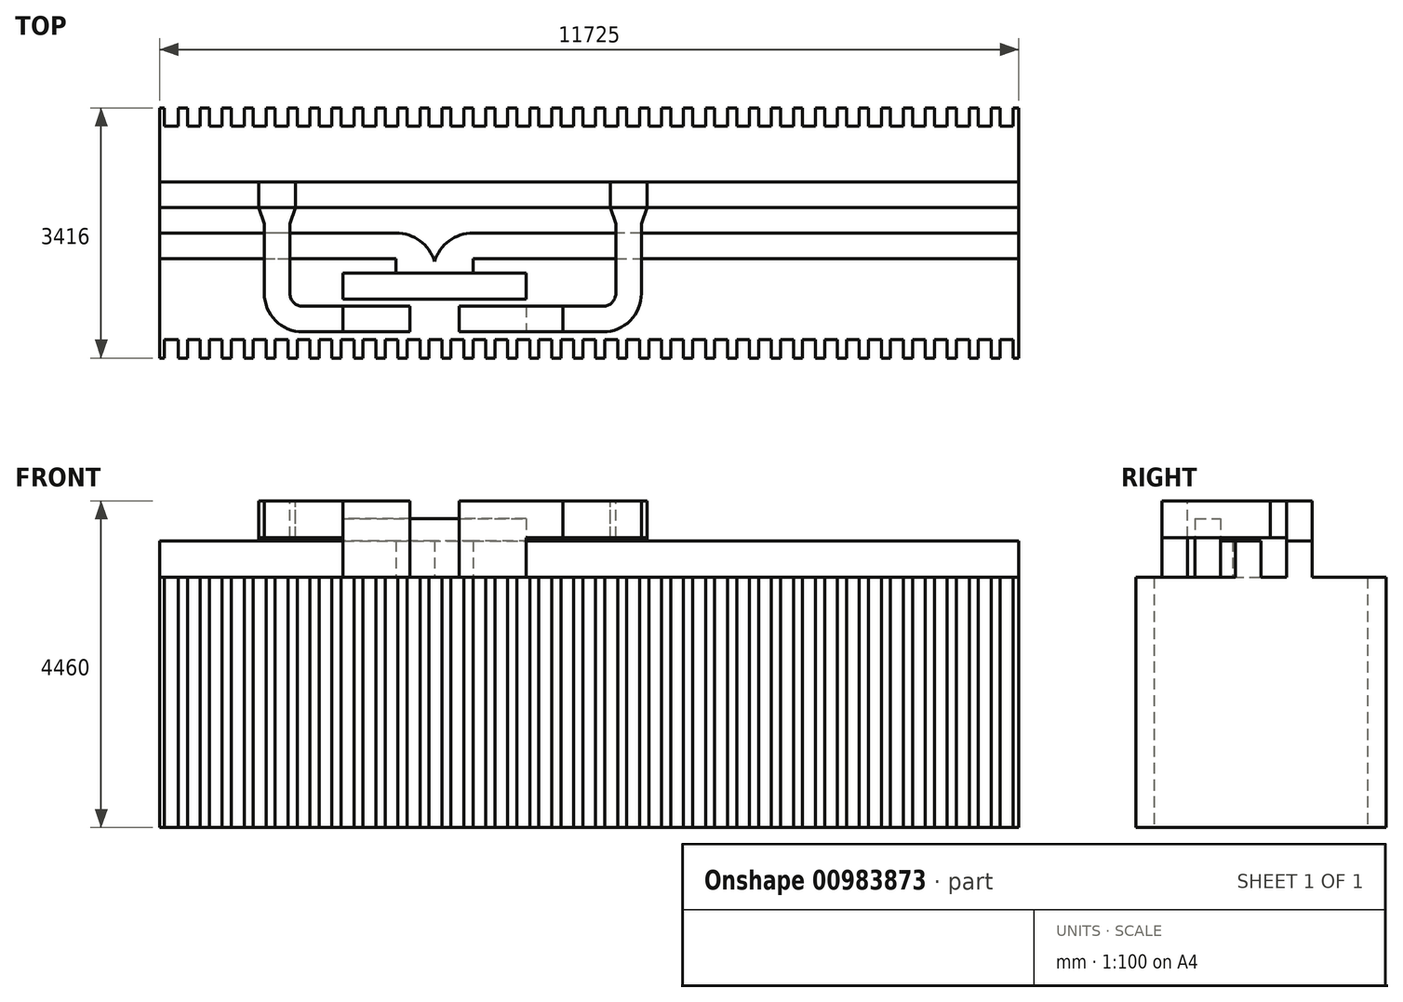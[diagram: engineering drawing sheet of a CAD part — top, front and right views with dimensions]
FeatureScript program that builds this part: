
annotation { "Feature Type Name" : "Feature", "Feature Type Description" : "" }
export const myFeature = defineFeature(function(context is Context, id is Id, definition is map)
    precondition{}
    {
        {
            var Q0;
            Q0=qCreatedBy(makeId("Top.planeOp"),FACE);
            var sketch = newSketch(context, id + "F0", { "sketchPlane" : qUnion([Q0])});
            skLineSegment(sketch, "E0.bottom", {"start": v(-25000, 7300) * mm, "end": v(25000, 7300) * mm});
            skLineSegment(sketch, "E0.top", {"start": v(-25000, -7300) * mm, "end": v(25000, -7300) * mm});
            skLineSegment(sketch, "E0.left", {"start": v(-25000, 7300) * mm, "end": v(-25000, -7300) * mm});
            skLineSegment(sketch, "E0.right", {"start": v(25000, 7300) * mm, "end": v(25000, -7300) * mm});
            skPoint(sketch, "E0.middle", {"position": v(0, 0) * mm});
            skSolve(sketch);
        }
        {
            var Q0;
            Q0=makeQuery(id+"F0.imprint","IMPRINT",FACE,{"disambiguationData":[TD([[makeQuery(id+"F0.imprint","IMPRINT",EDGE,{"derivedFrom":sQuery(id+"F0.wireOp",EDGE,"E0.bottom")}),-1.0]])]});
            var sketch = newSketch(context, id + "F1", { "sketchPlane" : qUnion([Q0])});
            skLineSegment(sketch, "E1", {"start": v(-20201.46, 5909) * mm, "end": v(-20138.96, 5909) * mm});
            skLineSegment(sketch, "E2", {"start": v(-20201.46, 5909) * mm, "end": v(-20201.46, 2493) * mm});
            skLineSegment(sketch, "E3", {"start": v(-20201.46, 2493) * mm, "end": v(-20138.96, 2493) * mm});
            skLineSegment(sketch, "E4", {"start": v(-8476.46, 2493) * mm, "end": v(-8476.46, 5909) * mm});
            skLineSegment(sketch, "E5.0", {"start": v(-20138.96, 5909) * mm, "end": v(-20138.96, 2493) * mm});
            skLineSegment(sketch, "E6.0", {"start": v(-19951.46, 5909) * mm, "end": v(-19951.46, 2493) * mm});
            skLineSegment(sketch, "E7.0", {"start": v(-19651.46, 5909) * mm, "end": v(-19651.46, 2493) * mm});
            skLineSegment(sketch, "E8.0", {"start": v(-19351.46, 5909) * mm, "end": v(-19351.46, 2493) * mm});
            skLineSegment(sketch, "E9.0", {"start": v(-19051.46, 5909) * mm, "end": v(-19051.46, 2493) * mm});
            skLineSegment(sketch, "E10.0", {"start": v(-18751.46, 5909) * mm, "end": v(-18751.46, 2493) * mm});
            skLineSegment(sketch, "E11.0", {"start": v(-18451.46, 5909) * mm, "end": v(-18451.46, 2493) * mm});
            skLineSegment(sketch, "E12.0", {"start": v(-18151.46, 5909) * mm, "end": v(-18151.46, 2493) * mm});
            skLineSegment(sketch, "E13.0", {"start": v(-17851.46, 5909) * mm, "end": v(-17851.46, 2493) * mm});
            skLineSegment(sketch, "E14.0", {"start": v(-17551.46, 5909) * mm, "end": v(-17551.46, 2493) * mm});
            skLineSegment(sketch, "E15.0", {"start": v(-17251.46, 5909) * mm, "end": v(-17251.46, 2493) * mm});
            skLineSegment(sketch, "E16.0", {"start": v(-16951.46, 5909) * mm, "end": v(-16951.46, 2493) * mm});
            skLineSegment(sketch, "E17.0", {"start": v(-16651.46, 5909) * mm, "end": v(-16651.46, 2493) * mm});
            skLineSegment(sketch, "E18.0", {"start": v(-16351.46, 5909) * mm, "end": v(-16351.46, 2493) * mm});
            skLineSegment(sketch, "E19.0", {"start": v(-16051.46, 5909) * mm, "end": v(-16051.46, 2493) * mm});
            skLineSegment(sketch, "E20.0", {"start": v(-15751.46, 5909) * mm, "end": v(-15751.46, 2493) * mm});
            skLineSegment(sketch, "E21.0", {"start": v(-25005, 7305) * mm, "end": v(-25005, -7305) * mm});
            skLineSegment(sketch, "E21.1", {"start": v(25005, 7305) * mm, "end": v(-25005, 7305) * mm});
            skLineSegment(sketch, "E21.2", {"start": v(25005, -7305) * mm, "end": v(25005, 7305) * mm});
            skLineSegment(sketch, "E21.3", {"start": v(-25005, -7305) * mm, "end": v(25005, -7305) * mm});
            skLineSegment(sketch, "E22.0", {"start": v(-15451.46, 5909) * mm, "end": v(-15451.46, 2493) * mm});
            skLineSegment(sketch, "E23.0", {"start": v(-15151.46, 5909) * mm, "end": v(-15151.46, 2493) * mm});
            skLineSegment(sketch, "E24.0", {"start": v(-14851.46, 5909) * mm, "end": v(-14851.46, 2493) * mm});
            skLineSegment(sketch, "E25.0", {"start": v(-14551.46, 5909) * mm, "end": v(-14551.46, 2493) * mm});
            skLineSegment(sketch, "E26.0", {"start": v(-14251.46, 5909) * mm, "end": v(-14251.46, 2493) * mm});
            skLineSegment(sketch, "E27.0", {"start": v(-13951.46, 5909) * mm, "end": v(-13951.46, 2493) * mm});
            skLineSegment(sketch, "E28.0", {"start": v(-13651.46, 5909) * mm, "end": v(-13651.46, 2493) * mm});
            skLineSegment(sketch, "E29.0", {"start": v(-13351.46, 5909) * mm, "end": v(-13351.46, 2493) * mm});
            skLineSegment(sketch, "E30.0", {"start": v(-13051.46, 5909) * mm, "end": v(-13051.46, 2493) * mm});
            skLineSegment(sketch, "E31.0", {"start": v(-12751.46, 5909) * mm, "end": v(-12751.46, 2493) * mm});
            skLineSegment(sketch, "E32.0", {"start": v(-12451.46, 5909) * mm, "end": v(-12451.46, 2493) * mm});
            skLineSegment(sketch, "E33.0", {"start": v(-12151.46, 5909) * mm, "end": v(-12151.46, 2493) * mm});
            skLineSegment(sketch, "E34.0", {"start": v(-11851.46, 5909) * mm, "end": v(-11851.46, 2493) * mm});
            skLineSegment(sketch, "E35.0", {"start": v(-11551.46, 5909) * mm, "end": v(-11551.46, 2493) * mm});
            skLineSegment(sketch, "E36.0", {"start": v(-11251.46, 5909) * mm, "end": v(-11251.46, 2493) * mm});
            skLineSegment(sketch, "E37.0", {"start": v(-10951.46, 5909) * mm, "end": v(-10951.46, 2493) * mm});
            skLineSegment(sketch, "E38.0", {"start": v(-10651.46, 5909) * mm, "end": v(-10651.46, 2493) * mm});
            skLineSegment(sketch, "E39.0", {"start": v(-10351.46, 5909) * mm, "end": v(-10351.46, 2493) * mm});
            skLineSegment(sketch, "E40.0", {"start": v(-10051.46, 5909) * mm, "end": v(-10051.46, 2493) * mm});
            skLineSegment(sketch, "E41.0", {"start": v(-9751.46, 5909) * mm, "end": v(-9751.46, 2493) * mm});
            skLineSegment(sketch, "E42.0", {"start": v(-9451.46, 5909) * mm, "end": v(-9451.46, 2493) * mm});
            skLineSegment(sketch, "E43.0", {"start": v(-9151.46, 5909) * mm, "end": v(-9151.46, 2493) * mm});
            skLineSegment(sketch, "E44.0", {"start": v(-8851.46, 5909) * mm, "end": v(-8851.46, 2493) * mm});
            skLineSegment(sketch, "E45.0", {"start": v(-8551.46, 5909) * mm, "end": v(-8551.46, 2493) * mm});
            skLineSegment(sketch, "E46.0", {"start": v(-19826.46, 5909) * mm, "end": v(-19826.46, 2493) * mm});
            skLineSegment(sketch, "E47.0", {"start": v(-19526.46, 5909) * mm, "end": v(-19526.46, 2493) * mm});
            skLineSegment(sketch, "E48.0", {"start": v(-19226.46, 5909) * mm, "end": v(-19226.46, 2493) * mm});
            skLineSegment(sketch, "E49.0", {"start": v(-18926.46, 5909) * mm, "end": v(-18926.46, 2493) * mm});
            skLineSegment(sketch, "E50.0", {"start": v(-18626.46, 5909) * mm, "end": v(-18626.46, 2493) * mm});
            skLineSegment(sketch, "E51.0", {"start": v(-18326.46, 5909) * mm, "end": v(-18326.46, 2493) * mm});
            skLineSegment(sketch, "E52.0", {"start": v(-18026.46, 5909) * mm, "end": v(-18026.46, 2493) * mm});
            skLineSegment(sketch, "E53.0", {"start": v(-17726.46, 5909) * mm, "end": v(-17726.46, 2493) * mm});
            skLineSegment(sketch, "E54.0", {"start": v(-17426.46, 5909) * mm, "end": v(-17426.46, 2493) * mm});
            skLineSegment(sketch, "E55.0", {"start": v(-17126.46, 5909) * mm, "end": v(-17126.46, 2493) * mm});
            skLineSegment(sketch, "E56.0", {"start": v(-16826.46, 5909) * mm, "end": v(-16826.46, 2493) * mm});
            skLineSegment(sketch, "E57.0", {"start": v(-16526.46, 5909) * mm, "end": v(-16526.46, 2493) * mm});
            skLineSegment(sketch, "E58.0", {"start": v(-16226.46, 5909) * mm, "end": v(-16226.46, 2493) * mm});
            skLineSegment(sketch, "E59.0", {"start": v(-15926.46, 5909) * mm, "end": v(-15926.46, 2493) * mm});
            skLineSegment(sketch, "E60.0", {"start": v(-15626.46, 5909) * mm, "end": v(-15626.46, 2493) * mm});
            skLineSegment(sketch, "E61.0", {"start": v(-15326.46, 5909) * mm, "end": v(-15326.46, 2493) * mm});
            skLineSegment(sketch, "E62.0", {"start": v(-15026.46, 5909) * mm, "end": v(-15026.46, 2493) * mm});
            skLineSegment(sketch, "E63.0", {"start": v(-14726.46, 5909) * mm, "end": v(-14726.46, 2493) * mm});
            skLineSegment(sketch, "E64.0", {"start": v(-14426.46, 5909) * mm, "end": v(-14426.46, 2493) * mm});
            skLineSegment(sketch, "E65.0", {"start": v(-14126.46, 5909) * mm, "end": v(-14126.46, 2493) * mm});
            skLineSegment(sketch, "E66.0", {"start": v(-13826.46, 5909) * mm, "end": v(-13826.46, 2493) * mm});
            skLineSegment(sketch, "E67.0", {"start": v(-13526.46, 5909) * mm, "end": v(-13526.46, 2493) * mm});
            skLineSegment(sketch, "E68.0", {"start": v(-13226.46, 5909) * mm, "end": v(-13226.46, 2493) * mm});
            skLineSegment(sketch, "E69.0", {"start": v(-12926.46, 5909) * mm, "end": v(-12926.46, 2493) * mm});
            skLineSegment(sketch, "E70.0", {"start": v(-12626.46, 5909) * mm, "end": v(-12626.46, 2493) * mm});
            skLineSegment(sketch, "E71.0", {"start": v(-12326.46, 5909) * mm, "end": v(-12326.46, 2493) * mm});
            skLineSegment(sketch, "E72.0", {"start": v(-12026.46, 5909) * mm, "end": v(-12026.46, 2493) * mm});
            skLineSegment(sketch, "E73.0", {"start": v(-11726.46, 5909) * mm, "end": v(-11726.46, 2493) * mm});
            skLineSegment(sketch, "E74.0", {"start": v(-11426.46, 5909) * mm, "end": v(-11426.46, 2493) * mm});
            skLineSegment(sketch, "E75.0", {"start": v(-11126.46, 5909) * mm, "end": v(-11126.46, 2493) * mm});
            skLineSegment(sketch, "E76.0", {"start": v(-10826.46, 5909) * mm, "end": v(-10826.46, 2493) * mm});
            skLineSegment(sketch, "E77.0", {"start": v(-10526.46, 5909) * mm, "end": v(-10526.46, 2493) * mm});
            skLineSegment(sketch, "E78.0", {"start": v(-10226.46, 5909) * mm, "end": v(-10226.46, 2493) * mm});
            skLineSegment(sketch, "E79.0", {"start": v(-9926.46, 5909) * mm, "end": v(-9926.46, 2493) * mm});
            skLineSegment(sketch, "E80.0", {"start": v(-9626.46, 5909) * mm, "end": v(-9626.46, 2493) * mm});
            skLineSegment(sketch, "E81.0", {"start": v(-9326.46, 5909) * mm, "end": v(-9326.46, 2493) * mm});
            skLineSegment(sketch, "E82.0", {"start": v(-9026.46, 5909) * mm, "end": v(-9026.46, 2493) * mm});
            skLineSegment(sketch, "E83.0", {"start": v(-8726.46, 5909) * mm, "end": v(-8726.46, 2493) * mm});
            skLineSegment(sketch, "E84", {"start": v(-20201.46, 5659) * mm, "end": v(-8476.46, 5659) * mm});
            skLineSegment(sketch, "E85", {"start": v(-20201.46, 2743) * mm, "end": v(-8476.46, 2743) * mm});
            skLineSegment(sketch, "E86.trimOffspring", {"start": v(-8551.46, 5909) * mm, "end": v(-8476.46, 5909) * mm});
            skLineSegment(sketch, "E87.trimOffspring", {"start": v(-8851.46, 5909) * mm, "end": v(-8726.46, 5909) * mm});
            skLineSegment(sketch, "E88.trimOffspring", {"start": v(-9151.46, 5909) * mm, "end": v(-9026.46, 5909) * mm});
            skLineSegment(sketch, "E89.trimOffspring", {"start": v(-9451.46, 5909) * mm, "end": v(-9326.46, 5909) * mm});
            skLineSegment(sketch, "E90.trimOffspring", {"start": v(-9751.46, 5909) * mm, "end": v(-9626.46, 5909) * mm});
            skLineSegment(sketch, "E91.trimOffspring", {"start": v(-10051.46, 5909) * mm, "end": v(-9926.46, 5909) * mm});
            skLineSegment(sketch, "E92.trimOffspring", {"start": v(-10351.46, 5909) * mm, "end": v(-10226.46, 5909) * mm});
            skLineSegment(sketch, "E93.trimOffspring", {"start": v(-10651.46, 5909) * mm, "end": v(-10526.46, 5909) * mm});
            skLineSegment(sketch, "E94.trimOffspring", {"start": v(-10951.46, 5909) * mm, "end": v(-10826.46, 5909) * mm});
            skLineSegment(sketch, "E95.trimOffspring", {"start": v(-11251.46, 5909) * mm, "end": v(-11126.46, 5909) * mm});
            skLineSegment(sketch, "E96.trimOffspring", {"start": v(-11551.46, 5909) * mm, "end": v(-11426.46, 5909) * mm});
            skLineSegment(sketch, "E97.trimOffspring", {"start": v(-11851.46, 5909) * mm, "end": v(-11726.46, 5909) * mm});
            skLineSegment(sketch, "E98.trimOffspring", {"start": v(-12151.46, 5909) * mm, "end": v(-12026.46, 5909) * mm});
            skLineSegment(sketch, "E99.trimOffspring", {"start": v(-12451.46, 5909) * mm, "end": v(-12326.46, 5909) * mm});
            skLineSegment(sketch, "E100.trimOffspring", {"start": v(-12751.46, 5909) * mm, "end": v(-12626.46, 5909) * mm});
            skLineSegment(sketch, "E101.trimOffspring", {"start": v(-13051.46, 5909) * mm, "end": v(-12926.46, 5909) * mm});
            skLineSegment(sketch, "E102.trimOffspring", {"start": v(-13351.46, 5909) * mm, "end": v(-13226.46, 5909) * mm});
            skLineSegment(sketch, "E103.trimOffspring", {"start": v(-13651.46, 5909) * mm, "end": v(-13526.46, 5909) * mm});
            skLineSegment(sketch, "E104.trimOffspring", {"start": v(-13951.46, 5909) * mm, "end": v(-13826.46, 5909) * mm});
            skLineSegment(sketch, "E105.trimOffspring", {"start": v(-14251.46, 5909) * mm, "end": v(-14126.46, 5909) * mm});
            skLineSegment(sketch, "E106.trimOffspring", {"start": v(-14551.46, 5909) * mm, "end": v(-14426.46, 5909) * mm});
            skLineSegment(sketch, "E107.trimOffspring", {"start": v(-14851.46, 5909) * mm, "end": v(-14726.46, 5909) * mm});
            skLineSegment(sketch, "E108.trimOffspring", {"start": v(-15151.46, 5909) * mm, "end": v(-15026.46, 5909) * mm});
            skLineSegment(sketch, "E109.trimOffspring", {"start": v(-15451.46, 5909) * mm, "end": v(-15326.46, 5909) * mm});
            skLineSegment(sketch, "E110.trimOffspring", {"start": v(-15751.46, 5909) * mm, "end": v(-15626.46, 5909) * mm});
            skLineSegment(sketch, "E111.trimOffspring", {"start": v(-16051.46, 5909) * mm, "end": v(-15926.46, 5909) * mm});
            skLineSegment(sketch, "E112.trimOffspring", {"start": v(-16351.46, 5909) * mm, "end": v(-16226.46, 5909) * mm});
            skLineSegment(sketch, "E113.trimOffspring", {"start": v(-16651.46, 5909) * mm, "end": v(-16526.46, 5909) * mm});
            skLineSegment(sketch, "E114.trimOffspring", {"start": v(-16951.46, 5909) * mm, "end": v(-16826.46, 5909) * mm});
            skLineSegment(sketch, "E115.trimOffspring", {"start": v(-17251.46, 5909) * mm, "end": v(-17126.46, 5909) * mm});
            skLineSegment(sketch, "E116.trimOffspring", {"start": v(-17551.46, 5909) * mm, "end": v(-17426.46, 5909) * mm});
            skLineSegment(sketch, "E117.trimOffspring", {"start": v(-17851.46, 5909) * mm, "end": v(-17726.46, 5909) * mm});
            skLineSegment(sketch, "E118.trimOffspring", {"start": v(-18151.46, 5909) * mm, "end": v(-18026.46, 5909) * mm});
            skLineSegment(sketch, "E119.trimOffspring", {"start": v(-18451.46, 5909) * mm, "end": v(-18326.46, 5909) * mm});
            skLineSegment(sketch, "E120.trimOffspring", {"start": v(-18751.46, 5909) * mm, "end": v(-18626.46, 5909) * mm});
            skLineSegment(sketch, "E121.trimOffspring", {"start": v(-19051.46, 5909) * mm, "end": v(-18926.46, 5909) * mm});
            skLineSegment(sketch, "E122.trimOffspring", {"start": v(-19351.46, 5909) * mm, "end": v(-19226.46, 5909) * mm});
            skLineSegment(sketch, "E123.trimOffspring", {"start": v(-19651.46, 5909) * mm, "end": v(-19526.46, 5909) * mm});
            skLineSegment(sketch, "E124.trimOffspring", {"start": v(-19951.46, 5909) * mm, "end": v(-19826.46, 5909) * mm});
            skLineSegment(sketch, "E125.trimOffspring", {"start": v(-19651.46, 2493) * mm, "end": v(-19526.46, 2493) * mm});
            skLineSegment(sketch, "E126.trimOffspring", {"start": v(-18751.46, 2493) * mm, "end": v(-18626.46, 2493) * mm});
            skLineSegment(sketch, "E127.trimOffspring", {"start": v(-17851.46, 2493) * mm, "end": v(-17726.46, 2493) * mm});
            skLineSegment(sketch, "E128.trimOffspring", {"start": v(-17251.46, 2493) * mm, "end": v(-17126.46, 2493) * mm});
            skLineSegment(sketch, "E129.trimOffspring", {"start": v(-16351.46, 2493) * mm, "end": v(-16226.46, 2493) * mm});
            skLineSegment(sketch, "E130.trimOffspring", {"start": v(-16951.46, 2493) * mm, "end": v(-16826.46, 2493) * mm});
            skLineSegment(sketch, "E131", {"start": v(-17551.46, 2493) * mm, "end": v(-17426.46, 2493) * mm});
            skLineSegment(sketch, "E132", {"start": v(-16651.46, 2493) * mm, "end": v(-16526.46, 2493) * mm});
            skLineSegment(sketch, "E133.trimOffspring", {"start": v(-15751.46, 2493) * mm, "end": v(-15626.46, 2493) * mm});
            skLineSegment(sketch, "E134.trimOffspring", {"start": v(-14551.46, 2493) * mm, "end": v(-14426.46, 2493) * mm});
            skLineSegment(sketch, "E135.trimOffspring", {"start": v(-15151.46, 2493) * mm, "end": v(-15026.46, 2493) * mm});
            skLineSegment(sketch, "E136.trimOffspring", {"start": v(-15451.46, 2493) * mm, "end": v(-15326.46, 2493) * mm});
            skLineSegment(sketch, "E137", {"start": v(-14851.46, 2493) * mm, "end": v(-14726.46, 2493) * mm});
            skLineSegment(sketch, "E138.trimOffspring", {"start": v(-13951.46, 2493) * mm, "end": v(-13826.46, 2493) * mm});
            skLineSegment(sketch, "E139.trimOffspring", {"start": v(-13351.46, 2493) * mm, "end": v(-13226.46, 2493) * mm});
            skLineSegment(sketch, "E140.trimOffspring", {"start": v(-13651.46, 2493) * mm, "end": v(-13526.46, 2493) * mm});
            skLineSegment(sketch, "E141", {"start": v(-14251.46, 2493) * mm, "end": v(-14126.46, 2493) * mm});
            skLineSegment(sketch, "E142.trimOffspring", {"start": v(-13051.46, 2493) * mm, "end": v(-12926.46, 2493) * mm});
            skLineSegment(sketch, "E143.trimOffspring", {"start": v(-12751.46, 2493) * mm, "end": v(-12626.46, 2493) * mm});
            skLineSegment(sketch, "E144.trimOffspring", {"start": v(-12151.46, 2493) * mm, "end": v(-12026.46, 2493) * mm});
            skLineSegment(sketch, "E145.trimOffspring", {"start": v(-11551.46, 2493) * mm, "end": v(-11426.46, 2493) * mm});
            skLineSegment(sketch, "E146.trimOffspring", {"start": v(-11851.46, 2493) * mm, "end": v(-11726.46, 2493) * mm});
            skLineSegment(sketch, "E147.trimOffspring", {"start": v(-11251.46, 2493) * mm, "end": v(-11126.46, 2493) * mm});
            skLineSegment(sketch, "E148.trimOffspring", {"start": v(-10951.46, 2493) * mm, "end": v(-10826.46, 2493) * mm});
            skLineSegment(sketch, "E149.trimOffspring", {"start": v(-10651.46, 2493) * mm, "end": v(-10526.46, 2493) * mm});
            skLineSegment(sketch, "E150.trimOffspring", {"start": v(-9751.46, 2493) * mm, "end": v(-9626.46, 2493) * mm});
            skLineSegment(sketch, "E151.trimOffspring", {"start": v(-8851.46, 2493) * mm, "end": v(-8726.46, 2493) * mm});
            skLineSegment(sketch, "E152", {"start": v(-10351.46, 2493) * mm, "end": v(-10226.46, 2493) * mm});
            skLineSegment(sketch, "E153", {"start": v(-10051.46, 2493) * mm, "end": v(-9926.46, 2493) * mm});
            skLineSegment(sketch, "E154", {"start": v(-9151.46, 2493) * mm, "end": v(-9026.46, 2493) * mm});
            skLineSegment(sketch, "E155.trimOffspring", {"start": v(-9451.46, 2493) * mm, "end": v(-9326.46, 2493) * mm});
            skLineSegment(sketch, "E156.trimOffspring", {"start": v(-8551.46, 2493) * mm, "end": v(-8476.46, 2493) * mm});
            skLineSegment(sketch, "E157.trimOffspring", {"start": v(-18451.46, 2493) * mm, "end": v(-18326.46, 2493) * mm});
            skLineSegment(sketch, "E158.trimOffspring", {"start": v(-19351.46, 2493) * mm, "end": v(-19226.46, 2493) * mm});
            skLineSegment(sketch, "E159", {"start": v(-19051.46, 2493) * mm, "end": v(-18926.46, 2493) * mm});
            skLineSegment(sketch, "E160", {"start": v(-18151.46, 2493) * mm, "end": v(-18026.46, 2493) * mm});
            skLineSegment(sketch, "E161", {"start": v(-16051.46, 2493) * mm, "end": v(-15926.46, 2493) * mm});
            skLineSegment(sketch, "E162", {"start": v(-19951.46, 2493) * mm, "end": v(-19826.46, 2493) * mm});
            skLineSegment(sketch, "E163", {"start": v(-12451.46, 2493) * mm, "end": v(-12326.46, 2493) * mm});
            skSolve(sketch);
        }
        {
            var Q0;
            {var subQ0=sQuery(id+"F1.wireOp",EDGE,"E88.trimOffspring");Q0=makeQuery(id+"F1.imprint","IMPRINT",FACE,{"disambiguationData":[TD([[makeQuery(id+"F1.imprint","IMPRINT",EDGE,{"derivedFrom":subQ0}),-1.0]])]});}
            var Q1;
            {var subQ0=sQuery(id+"F1.wireOp",EDGE,"E112.trimOffspring");Q1=makeQuery(id+"F1.imprint","IMPRINT",FACE,{"disambiguationData":[TD([[makeQuery(id+"F1.imprint","IMPRINT",EDGE,{"derivedFrom":subQ0}),-1.0]])]});}
            var Q2;
            {var subQ0=sQuery(id+"F1.wireOp",EDGE,"E84");var subQ1=sQuery(id+"F1.wireOp",EDGE,"E38.0");var subQ2=makeQuery(id+"F1.imprint","INTERSECT",VERTEX,{"derivedFrom":[subQ1,subQ0]});Q2=makeQuery(id+"F1.imprint","IMPRINT",FACE,{"disambiguationData":[TD([[makeQuery(id+"F1.imprint","IMPRINT",EDGE,{"disambiguationData":[TD([[subQ2,-1.0]])],"derivedFrom":subQ1}),1.0]])]});}
            var Q3;
            {var subQ0=sQuery(id+"F1.wireOp",EDGE,"E158.trimOffspring");Q3=makeQuery(id+"F1.imprint","IMPRINT",FACE,{"disambiguationData":[TD([[makeQuery(id+"F1.imprint","IMPRINT",EDGE,{"derivedFrom":subQ0}),1.0]])]});}
            var Q4;
            {var subQ0=sQuery(id+"F1.wireOp",EDGE,"E84");var subQ1=sQuery(id+"F1.wireOp",EDGE,"E18.0");var subQ2=makeQuery(id+"F1.imprint","INTERSECT",VERTEX,{"derivedFrom":[subQ1,subQ0]});Q4=makeQuery(id+"F1.imprint","IMPRINT",FACE,{"disambiguationData":[TD([[makeQuery(id+"F1.imprint","IMPRINT",EDGE,{"disambiguationData":[TD([[subQ2,-1.0]])],"derivedFrom":subQ1}),-1.0]])]});}
            var Q5;
            {var subQ0=sQuery(id+"F1.wireOp",EDGE,"E140.trimOffspring");Q5=makeQuery(id+"F1.imprint","IMPRINT",FACE,{"disambiguationData":[TD([[makeQuery(id+"F1.imprint","IMPRINT",EDGE,{"derivedFrom":subQ0}),1.0]])]});}
            var Q6;
            {var subQ0=sQuery(id+"F1.wireOp",EDGE,"E84");var subQ1=sQuery(id+"F1.wireOp",EDGE,"E35.0");var subQ2=makeQuery(id+"F1.imprint","INTERSECT",VERTEX,{"derivedFrom":[subQ1,subQ0]});Q6=makeQuery(id+"F1.imprint","IMPRINT",FACE,{"disambiguationData":[TD([[makeQuery(id+"F1.imprint","IMPRINT",EDGE,{"disambiguationData":[TD([[subQ2,-1.0]])],"derivedFrom":subQ1}),-1.0]])]});}
            var Q7;
            {var subQ0=sQuery(id+"F1.wireOp",EDGE,"E107.trimOffspring");Q7=makeQuery(id+"F1.imprint","IMPRINT",FACE,{"disambiguationData":[TD([[makeQuery(id+"F1.imprint","IMPRINT",EDGE,{"derivedFrom":subQ0}),-1.0]])]});}
            var Q8;
            {var subQ0=sQuery(id+"F1.wireOp",EDGE,"E129.trimOffspring");Q8=makeQuery(id+"F1.imprint","IMPRINT",FACE,{"disambiguationData":[TD([[makeQuery(id+"F1.imprint","IMPRINT",EDGE,{"derivedFrom":subQ0}),1.0]])]});}
            var Q9;
            {var subQ0=sQuery(id+"F1.wireOp",EDGE,"E120.trimOffspring");Q9=makeQuery(id+"F1.imprint","IMPRINT",FACE,{"disambiguationData":[TD([[makeQuery(id+"F1.imprint","IMPRINT",EDGE,{"derivedFrom":subQ0}),-1.0]])]});}
            var Q10;
            {var subQ0=sQuery(id+"F1.wireOp",EDGE,"E115.trimOffspring");Q10=makeQuery(id+"F1.imprint","IMPRINT",FACE,{"disambiguationData":[TD([[makeQuery(id+"F1.imprint","IMPRINT",EDGE,{"derivedFrom":subQ0}),-1.0]])]});}
            var Q11;
            {var subQ0=sQuery(id+"F1.wireOp",EDGE,"E138.trimOffspring");Q11=makeQuery(id+"F1.imprint","IMPRINT",FACE,{"disambiguationData":[TD([[makeQuery(id+"F1.imprint","IMPRINT",EDGE,{"derivedFrom":subQ0}),1.0]])]});}
            var Q12;
            {var subQ0=sQuery(id+"F1.wireOp",EDGE,"E84");var subQ1=sQuery(id+"F1.wireOp",EDGE,"E11.0");var subQ2=makeQuery(id+"F1.imprint","INTERSECT",VERTEX,{"derivedFrom":[subQ1,subQ0]});Q12=makeQuery(id+"F1.imprint","IMPRINT",FACE,{"disambiguationData":[TD([[makeQuery(id+"F1.imprint","IMPRINT",EDGE,{"disambiguationData":[TD([[subQ2,-1.0]])],"derivedFrom":subQ1}),1.0]])]});}
            var Q13;
            {var subQ0=sQuery(id+"F1.wireOp",EDGE,"E91.trimOffspring");Q13=makeQuery(id+"F1.imprint","IMPRINT",FACE,{"disambiguationData":[TD([[makeQuery(id+"F1.imprint","IMPRINT",EDGE,{"derivedFrom":subQ0}),-1.0]])]});}
            var Q14;
            {var subQ0=sQuery(id+"F1.wireOp",EDGE,"E84");var subQ1=sQuery(id+"F1.wireOp",EDGE,"E13.0");var subQ2=makeQuery(id+"F1.imprint","INTERSECT",VERTEX,{"derivedFrom":[subQ1,subQ0]});Q14=makeQuery(id+"F1.imprint","IMPRINT",FACE,{"disambiguationData":[TD([[makeQuery(id+"F1.imprint","IMPRINT",EDGE,{"disambiguationData":[TD([[subQ2,-1.0]])],"derivedFrom":subQ1}),-1.0]])]});}
            var Q15;
            {var subQ0=sQuery(id+"F1.wireOp",EDGE,"E84");var subQ1=sQuery(id+"F1.wireOp",EDGE,"E26.0");var subQ2=makeQuery(id+"F1.imprint","INTERSECT",VERTEX,{"derivedFrom":[subQ1,subQ0]});Q15=makeQuery(id+"F1.imprint","IMPRINT",FACE,{"disambiguationData":[TD([[makeQuery(id+"F1.imprint","IMPRINT",EDGE,{"disambiguationData":[TD([[subQ2,-1.0]])],"derivedFrom":subQ1}),-1.0]])]});}
            var Q16;
            {var subQ0=sQuery(id+"F1.wireOp",EDGE,"E121.trimOffspring");Q16=makeQuery(id+"F1.imprint","IMPRINT",FACE,{"disambiguationData":[TD([[makeQuery(id+"F1.imprint","IMPRINT",EDGE,{"derivedFrom":subQ0}),-1.0]])]});}
            var Q17;
            {var subQ0=sQuery(id+"F1.wireOp",EDGE,"E130.trimOffspring");Q17=makeQuery(id+"F1.imprint","IMPRINT",FACE,{"disambiguationData":[TD([[makeQuery(id+"F1.imprint","IMPRINT",EDGE,{"derivedFrom":subQ0}),1.0]])]});}
            var Q18;
            {var subQ0=sQuery(id+"F1.wireOp",EDGE,"E154");Q18=makeQuery(id+"F1.imprint","IMPRINT",FACE,{"disambiguationData":[TD([[makeQuery(id+"F1.imprint","IMPRINT",EDGE,{"derivedFrom":subQ0}),1.0]])]});}
            var Q19;
            {var subQ0=sQuery(id+"F1.wireOp",EDGE,"E151.trimOffspring");Q19=makeQuery(id+"F1.imprint","IMPRINT",FACE,{"disambiguationData":[TD([[makeQuery(id+"F1.imprint","IMPRINT",EDGE,{"derivedFrom":subQ0}),1.0]])]});}
            var Q20;
            {var subQ0=sQuery(id+"F1.wireOp",EDGE,"E84");var subQ1=sQuery(id+"F1.wireOp",EDGE,"E30.0");var subQ2=makeQuery(id+"F1.imprint","INTERSECT",VERTEX,{"derivedFrom":[subQ1,subQ0]});Q20=makeQuery(id+"F1.imprint","IMPRINT",FACE,{"disambiguationData":[TD([[makeQuery(id+"F1.imprint","IMPRINT",EDGE,{"disambiguationData":[TD([[subQ2,-1.0]])],"derivedFrom":subQ1}),-1.0]])]});}
            var Q21;
            {var subQ0=sQuery(id+"F1.wireOp",EDGE,"E84");var subQ1=sQuery(id+"F1.wireOp",EDGE,"E19.0");var subQ2=makeQuery(id+"F1.imprint","INTERSECT",VERTEX,{"derivedFrom":[subQ1,subQ0]});Q21=makeQuery(id+"F1.imprint","IMPRINT",FACE,{"disambiguationData":[TD([[makeQuery(id+"F1.imprint","IMPRINT",EDGE,{"disambiguationData":[TD([[subQ2,-1.0]])],"derivedFrom":subQ1}),1.0]])]});}
            var Q22;
            {var subQ0=sQuery(id+"F1.wireOp",EDGE,"E84");var subQ1=sQuery(id+"F1.wireOp",EDGE,"E14.0");var subQ2=makeQuery(id+"F1.imprint","INTERSECT",VERTEX,{"derivedFrom":[subQ1,subQ0]});Q22=makeQuery(id+"F1.imprint","IMPRINT",FACE,{"disambiguationData":[TD([[makeQuery(id+"F1.imprint","IMPRINT",EDGE,{"disambiguationData":[TD([[subQ2,-1.0]])],"derivedFrom":subQ1}),-1.0]])]});}
            var Q23;
            {var subQ0=sQuery(id+"F1.wireOp",EDGE,"E84");var subQ1=sQuery(id+"F1.wireOp",EDGE,"E12.0");var subQ2=makeQuery(id+"F1.imprint","INTERSECT",VERTEX,{"derivedFrom":[subQ1,subQ0]});Q23=makeQuery(id+"F1.imprint","IMPRINT",FACE,{"disambiguationData":[TD([[makeQuery(id+"F1.imprint","IMPRINT",EDGE,{"disambiguationData":[TD([[subQ2,-1.0]])],"derivedFrom":subQ1}),1.0]])]});}
            var Q24;
            {var subQ0=sQuery(id+"F1.wireOp",EDGE,"E143.trimOffspring");Q24=makeQuery(id+"F1.imprint","IMPRINT",FACE,{"disambiguationData":[TD([[makeQuery(id+"F1.imprint","IMPRINT",EDGE,{"derivedFrom":subQ0}),1.0]])]});}
            var Q25;
            {var subQ0=sQuery(id+"F1.wireOp",EDGE,"E161");Q25=makeQuery(id+"F1.imprint","IMPRINT",FACE,{"disambiguationData":[TD([[makeQuery(id+"F1.imprint","IMPRINT",EDGE,{"derivedFrom":subQ0}),1.0]])]});}
            var Q26;
            {var subQ0=sQuery(id+"F1.wireOp",EDGE,"E100.trimOffspring");Q26=makeQuery(id+"F1.imprint","IMPRINT",FACE,{"disambiguationData":[TD([[makeQuery(id+"F1.imprint","IMPRINT",EDGE,{"derivedFrom":subQ0}),-1.0]])]});}
            var Q27;
            {var subQ0=sQuery(id+"F1.wireOp",EDGE,"E84");var subQ1=sQuery(id+"F1.wireOp",EDGE,"E15.0");var subQ2=makeQuery(id+"F1.imprint","INTERSECT",VERTEX,{"derivedFrom":[subQ1,subQ0]});Q27=makeQuery(id+"F1.imprint","IMPRINT",FACE,{"disambiguationData":[TD([[makeQuery(id+"F1.imprint","IMPRINT",EDGE,{"disambiguationData":[TD([[subQ2,-1.0]])],"derivedFrom":subQ1}),-1.0]])]});}
            var Q28;
            {var subQ0=sQuery(id+"F1.wireOp",EDGE,"E84");var subQ1=sQuery(id+"F1.wireOp",EDGE,"E39.0");var subQ2=makeQuery(id+"F1.imprint","INTERSECT",VERTEX,{"derivedFrom":[subQ1,subQ0]});Q28=makeQuery(id+"F1.imprint","IMPRINT",FACE,{"disambiguationData":[TD([[makeQuery(id+"F1.imprint","IMPRINT",EDGE,{"disambiguationData":[TD([[subQ2,-1.0]])],"derivedFrom":subQ1}),1.0]])]});}
            var Q29;
            {var subQ0=sQuery(id+"F1.wireOp",EDGE,"E84");var subQ1=sQuery(id+"F1.wireOp",EDGE,"E36.0");var subQ2=makeQuery(id+"F1.imprint","INTERSECT",VERTEX,{"derivedFrom":[subQ1,subQ0]});Q29=makeQuery(id+"F1.imprint","IMPRINT",FACE,{"disambiguationData":[TD([[makeQuery(id+"F1.imprint","IMPRINT",EDGE,{"disambiguationData":[TD([[subQ2,-1.0]])],"derivedFrom":subQ1}),1.0]])]});}
            var Q30;
            {var subQ0=sQuery(id+"F1.wireOp",EDGE,"E84");var subQ1=sQuery(id+"F1.wireOp",EDGE,"E40.0");var subQ2=makeQuery(id+"F1.imprint","INTERSECT",VERTEX,{"derivedFrom":[subQ1,subQ0]});Q30=makeQuery(id+"F1.imprint","IMPRINT",FACE,{"disambiguationData":[TD([[makeQuery(id+"F1.imprint","IMPRINT",EDGE,{"disambiguationData":[TD([[subQ2,-1.0]])],"derivedFrom":subQ1}),1.0]])]});}
            var Q31;
            {var subQ0=sQuery(id+"F1.wireOp",EDGE,"E118.trimOffspring");Q31=makeQuery(id+"F1.imprint","IMPRINT",FACE,{"disambiguationData":[TD([[makeQuery(id+"F1.imprint","IMPRINT",EDGE,{"derivedFrom":subQ0}),-1.0]])]});}
            var Q32;
            {var subQ0=sQuery(id+"F1.wireOp",EDGE,"E84");var subQ1=sQuery(id+"F1.wireOp",EDGE,"E10.0");var subQ2=makeQuery(id+"F1.imprint","INTERSECT",VERTEX,{"derivedFrom":[subQ1,subQ0]});Q32=makeQuery(id+"F1.imprint","IMPRINT",FACE,{"disambiguationData":[TD([[makeQuery(id+"F1.imprint","IMPRINT",EDGE,{"disambiguationData":[TD([[subQ2,-1.0]])],"derivedFrom":subQ1}),-1.0]])]});}
            var Q33;
            {var subQ0=sQuery(id+"F1.wireOp",EDGE,"E84");var subQ1=sQuery(id+"F1.wireOp",EDGE,"E19.0");var subQ2=makeQuery(id+"F1.imprint","INTERSECT",VERTEX,{"derivedFrom":[subQ1,subQ0]});Q33=makeQuery(id+"F1.imprint","IMPRINT",FACE,{"disambiguationData":[TD([[makeQuery(id+"F1.imprint","IMPRINT",EDGE,{"disambiguationData":[TD([[subQ2,-1.0]])],"derivedFrom":subQ1}),-1.0]])]});}
            var Q34;
            {var subQ0=sQuery(id+"F1.wireOp",EDGE,"E84");var subQ1=sQuery(id+"F1.wireOp",EDGE,"E29.0");var subQ2=makeQuery(id+"F1.imprint","INTERSECT",VERTEX,{"derivedFrom":[subQ1,subQ0]});Q34=makeQuery(id+"F1.imprint","IMPRINT",FACE,{"disambiguationData":[TD([[makeQuery(id+"F1.imprint","IMPRINT",EDGE,{"disambiguationData":[TD([[subQ2,-1.0]])],"derivedFrom":subQ1}),-1.0]])]});}
            var Q35;
            {var subQ0=sQuery(id+"F1.wireOp",EDGE,"E84");var subQ1=sQuery(id+"F1.wireOp",EDGE,"E9.0");var subQ2=makeQuery(id+"F1.imprint","INTERSECT",VERTEX,{"derivedFrom":[subQ1,subQ0]});Q35=makeQuery(id+"F1.imprint","IMPRINT",FACE,{"disambiguationData":[TD([[makeQuery(id+"F1.imprint","IMPRINT",EDGE,{"disambiguationData":[TD([[subQ2,-1.0]])],"derivedFrom":subQ1}),-1.0]])]});}
            var Q36;
            {var subQ0=sQuery(id+"F1.wireOp",EDGE,"E102.trimOffspring");Q36=makeQuery(id+"F1.imprint","IMPRINT",FACE,{"disambiguationData":[TD([[makeQuery(id+"F1.imprint","IMPRINT",EDGE,{"derivedFrom":subQ0}),-1.0]])]});}
            var Q37;
            {var subQ0=sQuery(id+"F1.wireOp",EDGE,"E99.trimOffspring");Q37=makeQuery(id+"F1.imprint","IMPRINT",FACE,{"disambiguationData":[TD([[makeQuery(id+"F1.imprint","IMPRINT",EDGE,{"derivedFrom":subQ0}),-1.0]])]});}
            var Q38;
            {var subQ0=sQuery(id+"F1.wireOp",EDGE,"E117.trimOffspring");Q38=makeQuery(id+"F1.imprint","IMPRINT",FACE,{"disambiguationData":[TD([[makeQuery(id+"F1.imprint","IMPRINT",EDGE,{"derivedFrom":subQ0}),-1.0]])]});}
            var Q39;
            {var subQ0=sQuery(id+"F1.wireOp",EDGE,"E84");var subQ1=sQuery(id+"F1.wireOp",EDGE,"E17.0");var subQ2=makeQuery(id+"F1.imprint","INTERSECT",VERTEX,{"derivedFrom":[subQ1,subQ0]});Q39=makeQuery(id+"F1.imprint","IMPRINT",FACE,{"disambiguationData":[TD([[makeQuery(id+"F1.imprint","IMPRINT",EDGE,{"disambiguationData":[TD([[subQ2,-1.0]])],"derivedFrom":subQ1}),-1.0]])]});}
            var Q40;
            {var subQ0=sQuery(id+"F1.wireOp",EDGE,"E84");var subQ1=sQuery(id+"F1.wireOp",EDGE,"E33.0");var subQ2=makeQuery(id+"F1.imprint","INTERSECT",VERTEX,{"derivedFrom":[subQ1,subQ0]});Q40=makeQuery(id+"F1.imprint","IMPRINT",FACE,{"disambiguationData":[TD([[makeQuery(id+"F1.imprint","IMPRINT",EDGE,{"disambiguationData":[TD([[subQ2,-1.0]])],"derivedFrom":subQ1}),-1.0]])]});}
            var Q41;
            {var subQ0=sQuery(id+"F1.wireOp",EDGE,"E146.trimOffspring");Q41=makeQuery(id+"F1.imprint","IMPRINT",FACE,{"disambiguationData":[TD([[makeQuery(id+"F1.imprint","IMPRINT",EDGE,{"derivedFrom":subQ0}),1.0]])]});}
            var Q42;
            {var subQ0=sQuery(id+"F1.wireOp",EDGE,"E95.trimOffspring");Q42=makeQuery(id+"F1.imprint","IMPRINT",FACE,{"disambiguationData":[TD([[makeQuery(id+"F1.imprint","IMPRINT",EDGE,{"derivedFrom":subQ0}),-1.0]])]});}
            var Q43;
            {var subQ0=sQuery(id+"F1.wireOp",EDGE,"E134.trimOffspring");Q43=makeQuery(id+"F1.imprint","IMPRINT",FACE,{"disambiguationData":[TD([[makeQuery(id+"F1.imprint","IMPRINT",EDGE,{"derivedFrom":subQ0}),1.0]])]});}
            var Q44;
            {var subQ0=sQuery(id+"F1.wireOp",EDGE,"E122.trimOffspring");Q44=makeQuery(id+"F1.imprint","IMPRINT",FACE,{"disambiguationData":[TD([[makeQuery(id+"F1.imprint","IMPRINT",EDGE,{"derivedFrom":subQ0}),-1.0]])]});}
            var Q45;
            {var subQ0=sQuery(id+"F1.wireOp",EDGE,"E105.trimOffspring");Q45=makeQuery(id+"F1.imprint","IMPRINT",FACE,{"disambiguationData":[TD([[makeQuery(id+"F1.imprint","IMPRINT",EDGE,{"derivedFrom":subQ0}),-1.0]])]});}
            var Q46;
            {var subQ0=sQuery(id+"F1.wireOp",EDGE,"E84");var subQ1=sQuery(id+"F1.wireOp",EDGE,"E31.0");var subQ2=makeQuery(id+"F1.imprint","INTERSECT",VERTEX,{"derivedFrom":[subQ1,subQ0]});Q46=makeQuery(id+"F1.imprint","IMPRINT",FACE,{"disambiguationData":[TD([[makeQuery(id+"F1.imprint","IMPRINT",EDGE,{"disambiguationData":[TD([[subQ2,-1.0]])],"derivedFrom":subQ1}),-1.0]])]});}
            var Q47;
            {var subQ0=sQuery(id+"F1.wireOp",EDGE,"E84");var subQ1=sQuery(id+"F1.wireOp",EDGE,"E24.0");var subQ2=makeQuery(id+"F1.imprint","INTERSECT",VERTEX,{"derivedFrom":[subQ1,subQ0]});Q47=makeQuery(id+"F1.imprint","IMPRINT",FACE,{"disambiguationData":[TD([[makeQuery(id+"F1.imprint","IMPRINT",EDGE,{"disambiguationData":[TD([[subQ2,-1.0]])],"derivedFrom":subQ1}),1.0]])]});}
            var Q48;
            {var subQ0=sQuery(id+"F1.wireOp",EDGE,"E84");var subQ1=sQuery(id+"F1.wireOp",EDGE,"E43.0");var subQ2=makeQuery(id+"F1.imprint","INTERSECT",VERTEX,{"derivedFrom":[subQ1,subQ0]});Q48=makeQuery(id+"F1.imprint","IMPRINT",FACE,{"disambiguationData":[TD([[makeQuery(id+"F1.imprint","IMPRINT",EDGE,{"disambiguationData":[TD([[subQ2,-1.0]])],"derivedFrom":subQ1}),1.0]])]});}
            var Q49;
            {var subQ0=sQuery(id+"F1.wireOp",EDGE,"E123.trimOffspring");Q49=makeQuery(id+"F1.imprint","IMPRINT",FACE,{"disambiguationData":[TD([[makeQuery(id+"F1.imprint","IMPRINT",EDGE,{"derivedFrom":subQ0}),-1.0]])]});}
            var Q50;
            {var subQ0=sQuery(id+"F1.wireOp",EDGE,"E84");var subQ1=sQuery(id+"F1.wireOp",EDGE,"E43.0");var subQ2=makeQuery(id+"F1.imprint","INTERSECT",VERTEX,{"derivedFrom":[subQ1,subQ0]});Q50=makeQuery(id+"F1.imprint","IMPRINT",FACE,{"disambiguationData":[TD([[makeQuery(id+"F1.imprint","IMPRINT",EDGE,{"disambiguationData":[TD([[subQ2,-1.0]])],"derivedFrom":subQ1}),-1.0]])]});}
            var Q51;
            {var subQ0=sQuery(id+"F1.wireOp",EDGE,"E84");var subQ1=sQuery(id+"F1.wireOp",EDGE,"E32.0");var subQ2=makeQuery(id+"F1.imprint","INTERSECT",VERTEX,{"derivedFrom":[subQ1,subQ0]});Q51=makeQuery(id+"F1.imprint","IMPRINT",FACE,{"disambiguationData":[TD([[makeQuery(id+"F1.imprint","IMPRINT",EDGE,{"disambiguationData":[TD([[subQ2,-1.0]])],"derivedFrom":subQ1}),1.0]])]});}
            var Q52;
            {var subQ0=sQuery(id+"F1.wireOp",EDGE,"E133.trimOffspring");Q52=makeQuery(id+"F1.imprint","IMPRINT",FACE,{"disambiguationData":[TD([[makeQuery(id+"F1.imprint","IMPRINT",EDGE,{"derivedFrom":subQ0}),1.0]])]});}
            var Q53;
            {var subQ0=sQuery(id+"F1.wireOp",EDGE,"E84");var subQ1=sQuery(id+"F1.wireOp",EDGE,"E37.0");var subQ2=makeQuery(id+"F1.imprint","INTERSECT",VERTEX,{"derivedFrom":[subQ1,subQ0]});Q53=makeQuery(id+"F1.imprint","IMPRINT",FACE,{"disambiguationData":[TD([[makeQuery(id+"F1.imprint","IMPRINT",EDGE,{"disambiguationData":[TD([[subQ2,-1.0]])],"derivedFrom":subQ1}),1.0]])]});}
            var Q54;
            {var subQ0=sQuery(id+"F1.wireOp",EDGE,"E141");Q54=makeQuery(id+"F1.imprint","IMPRINT",FACE,{"disambiguationData":[TD([[makeQuery(id+"F1.imprint","IMPRINT",EDGE,{"derivedFrom":subQ0}),1.0]])]});}
            var Q55;
            {var subQ0=sQuery(id+"F1.wireOp",EDGE,"E84");var subQ1=sQuery(id+"F1.wireOp",EDGE,"E17.0");var subQ2=makeQuery(id+"F1.imprint","INTERSECT",VERTEX,{"derivedFrom":[subQ1,subQ0]});Q55=makeQuery(id+"F1.imprint","IMPRINT",FACE,{"disambiguationData":[TD([[makeQuery(id+"F1.imprint","IMPRINT",EDGE,{"disambiguationData":[TD([[subQ2,-1.0]])],"derivedFrom":subQ1}),1.0]])]});}
            var Q56;
            {var subQ0=sQuery(id+"F1.wireOp",EDGE,"E127.trimOffspring");Q56=makeQuery(id+"F1.imprint","IMPRINT",FACE,{"disambiguationData":[TD([[makeQuery(id+"F1.imprint","IMPRINT",EDGE,{"derivedFrom":subQ0}),1.0]])]});}
            var Q57;
            {var subQ0=sQuery(id+"F1.wireOp",EDGE,"E84");var subQ1=sQuery(id+"F1.wireOp",EDGE,"E8.0");var subQ2=makeQuery(id+"F1.imprint","INTERSECT",VERTEX,{"derivedFrom":[subQ1,subQ0]});Q57=makeQuery(id+"F1.imprint","IMPRINT",FACE,{"disambiguationData":[TD([[makeQuery(id+"F1.imprint","IMPRINT",EDGE,{"disambiguationData":[TD([[subQ2,-1.0]])],"derivedFrom":subQ1}),-1.0]])]});}
            var Q58;
            {var subQ0=sQuery(id+"F1.wireOp",EDGE,"E84");var subQ1=sQuery(id+"F1.wireOp",EDGE,"E35.0");var subQ2=makeQuery(id+"F1.imprint","INTERSECT",VERTEX,{"derivedFrom":[subQ1,subQ0]});Q58=makeQuery(id+"F1.imprint","IMPRINT",FACE,{"disambiguationData":[TD([[makeQuery(id+"F1.imprint","IMPRINT",EDGE,{"disambiguationData":[TD([[subQ2,-1.0]])],"derivedFrom":subQ1}),1.0]])]});}
            var Q59;
            {var subQ0=sQuery(id+"F1.wireOp",EDGE,"E84");var subQ1=sQuery(id+"F1.wireOp",EDGE,"E27.0");var subQ2=makeQuery(id+"F1.imprint","INTERSECT",VERTEX,{"derivedFrom":[subQ1,subQ0]});Q59=makeQuery(id+"F1.imprint","IMPRINT",FACE,{"disambiguationData":[TD([[makeQuery(id+"F1.imprint","IMPRINT",EDGE,{"disambiguationData":[TD([[subQ2,-1.0]])],"derivedFrom":subQ1}),1.0]])]});}
            var Q60;
            {var subQ0=sQuery(id+"F1.wireOp",EDGE,"E84");var subQ1=sQuery(id+"F1.wireOp",EDGE,"E42.0");var subQ2=makeQuery(id+"F1.imprint","INTERSECT",VERTEX,{"derivedFrom":[subQ1,subQ0]});Q60=makeQuery(id+"F1.imprint","IMPRINT",FACE,{"disambiguationData":[TD([[makeQuery(id+"F1.imprint","IMPRINT",EDGE,{"disambiguationData":[TD([[subQ2,-1.0]])],"derivedFrom":subQ1}),-1.0]])]});}
            var Q61;
            {var subQ0=sQuery(id+"F1.wireOp",EDGE,"E93.trimOffspring");Q61=makeQuery(id+"F1.imprint","IMPRINT",FACE,{"disambiguationData":[TD([[makeQuery(id+"F1.imprint","IMPRINT",EDGE,{"derivedFrom":subQ0}),-1.0]])]});}
            var Q62;
            {var subQ0=sQuery(id+"F1.wireOp",EDGE,"E84");var subQ1=sQuery(id+"F1.wireOp",EDGE,"E28.0");var subQ2=makeQuery(id+"F1.imprint","INTERSECT",VERTEX,{"derivedFrom":[subQ1,subQ0]});Q62=makeQuery(id+"F1.imprint","IMPRINT",FACE,{"disambiguationData":[TD([[makeQuery(id+"F1.imprint","IMPRINT",EDGE,{"disambiguationData":[TD([[subQ2,-1.0]])],"derivedFrom":subQ1}),-1.0]])]});}
            var Q63;
            {var subQ0=sQuery(id+"F1.wireOp",EDGE,"E84");var subQ1=sQuery(id+"F1.wireOp",EDGE,"E12.0");var subQ2=makeQuery(id+"F1.imprint","INTERSECT",VERTEX,{"derivedFrom":[subQ1,subQ0]});Q63=makeQuery(id+"F1.imprint","IMPRINT",FACE,{"disambiguationData":[TD([[makeQuery(id+"F1.imprint","IMPRINT",EDGE,{"disambiguationData":[TD([[subQ2,-1.0]])],"derivedFrom":subQ1}),-1.0]])]});}
            var Q64;
            {var subQ0=sQuery(id+"F1.wireOp",EDGE,"E84");var subQ1=sQuery(id+"F1.wireOp",EDGE,"E26.0");var subQ2=makeQuery(id+"F1.imprint","INTERSECT",VERTEX,{"derivedFrom":[subQ1,subQ0]});Q64=makeQuery(id+"F1.imprint","IMPRINT",FACE,{"disambiguationData":[TD([[makeQuery(id+"F1.imprint","IMPRINT",EDGE,{"disambiguationData":[TD([[subQ2,-1.0]])],"derivedFrom":subQ1}),1.0]])]});}
            var Q65;
            {var subQ0=sQuery(id+"F1.wireOp",EDGE,"E148.trimOffspring");Q65=makeQuery(id+"F1.imprint","IMPRINT",FACE,{"disambiguationData":[TD([[makeQuery(id+"F1.imprint","IMPRINT",EDGE,{"derivedFrom":subQ0}),1.0]])]});}
            var Q66;
            {var subQ0=sQuery(id+"F1.wireOp",EDGE,"E142.trimOffspring");Q66=makeQuery(id+"F1.imprint","IMPRINT",FACE,{"disambiguationData":[TD([[makeQuery(id+"F1.imprint","IMPRINT",EDGE,{"derivedFrom":subQ0}),1.0]])]});}
            var Q67;
            {var subQ0=sQuery(id+"F1.wireOp",EDGE,"E106.trimOffspring");Q67=makeQuery(id+"F1.imprint","IMPRINT",FACE,{"disambiguationData":[TD([[makeQuery(id+"F1.imprint","IMPRINT",EDGE,{"derivedFrom":subQ0}),-1.0]])]});}
            var Q68;
            {var subQ0=sQuery(id+"F1.wireOp",EDGE,"E84");var subQ1=sQuery(id+"F1.wireOp",EDGE,"E28.0");var subQ2=makeQuery(id+"F1.imprint","INTERSECT",VERTEX,{"derivedFrom":[subQ1,subQ0]});Q68=makeQuery(id+"F1.imprint","IMPRINT",FACE,{"disambiguationData":[TD([[makeQuery(id+"F1.imprint","IMPRINT",EDGE,{"disambiguationData":[TD([[subQ2,-1.0]])],"derivedFrom":subQ1}),1.0]])]});}
            var Q69;
            {var subQ0=sQuery(id+"F1.wireOp",EDGE,"E92.trimOffspring");Q69=makeQuery(id+"F1.imprint","IMPRINT",FACE,{"disambiguationData":[TD([[makeQuery(id+"F1.imprint","IMPRINT",EDGE,{"derivedFrom":subQ0}),-1.0]])]});}
            var Q70;
            {var subQ0=sQuery(id+"F1.wireOp",EDGE,"E84");var subQ1=sQuery(id+"F1.wireOp",EDGE,"E7.0");var subQ2=makeQuery(id+"F1.imprint","INTERSECT",VERTEX,{"derivedFrom":[subQ1,subQ0]});Q70=makeQuery(id+"F1.imprint","IMPRINT",FACE,{"disambiguationData":[TD([[makeQuery(id+"F1.imprint","IMPRINT",EDGE,{"disambiguationData":[TD([[subQ2,-1.0]])],"derivedFrom":subQ1}),-1.0]])]});}
            var Q71;
            {var subQ0=sQuery(id+"F1.wireOp",EDGE,"E84");var subQ1=sQuery(id+"F1.wireOp",EDGE,"E31.0");var subQ2=makeQuery(id+"F1.imprint","INTERSECT",VERTEX,{"derivedFrom":[subQ1,subQ0]});Q71=makeQuery(id+"F1.imprint","IMPRINT",FACE,{"disambiguationData":[TD([[makeQuery(id+"F1.imprint","IMPRINT",EDGE,{"disambiguationData":[TD([[subQ2,-1.0]])],"derivedFrom":subQ1}),1.0]])]});}
            var Q72;
            {var subQ0=sQuery(id+"F1.wireOp",EDGE,"E152");Q72=makeQuery(id+"F1.imprint","IMPRINT",FACE,{"disambiguationData":[TD([[makeQuery(id+"F1.imprint","IMPRINT",EDGE,{"derivedFrom":subQ0}),1.0]])]});}
            var Q73;
            {var subQ0=sQuery(id+"F1.wireOp",EDGE,"E87.trimOffspring");Q73=makeQuery(id+"F1.imprint","IMPRINT",FACE,{"disambiguationData":[TD([[makeQuery(id+"F1.imprint","IMPRINT",EDGE,{"derivedFrom":subQ0}),-1.0]])]});}
            var Q74;
            {var subQ0=sQuery(id+"F1.wireOp",EDGE,"E84");var subQ1=sQuery(id+"F1.wireOp",EDGE,"E22.0");var subQ2=makeQuery(id+"F1.imprint","INTERSECT",VERTEX,{"derivedFrom":[subQ1,subQ0]});Q74=makeQuery(id+"F1.imprint","IMPRINT",FACE,{"disambiguationData":[TD([[makeQuery(id+"F1.imprint","IMPRINT",EDGE,{"disambiguationData":[TD([[subQ2,-1.0]])],"derivedFrom":subQ1}),-1.0]])]});}
            var Q75;
            {var subQ0=sQuery(id+"F1.wireOp",EDGE,"E84");var subQ1=sQuery(id+"F1.wireOp",EDGE,"E44.0");var subQ2=makeQuery(id+"F1.imprint","INTERSECT",VERTEX,{"derivedFrom":[subQ1,subQ0]});Q75=makeQuery(id+"F1.imprint","IMPRINT",FACE,{"disambiguationData":[TD([[makeQuery(id+"F1.imprint","IMPRINT",EDGE,{"disambiguationData":[TD([[subQ2,-1.0]])],"derivedFrom":subQ1}),1.0]])]});}
            var Q76;
            {var subQ0=sQuery(id+"F1.wireOp",EDGE,"E84");var subQ1=sQuery(id+"F1.wireOp",EDGE,"E18.0");var subQ2=makeQuery(id+"F1.imprint","INTERSECT",VERTEX,{"derivedFrom":[subQ1,subQ0]});Q76=makeQuery(id+"F1.imprint","IMPRINT",FACE,{"disambiguationData":[TD([[makeQuery(id+"F1.imprint","IMPRINT",EDGE,{"disambiguationData":[TD([[subQ2,-1.0]])],"derivedFrom":subQ1}),1.0]])]});}
            var Q77;
            {var subQ0=sQuery(id+"F1.wireOp",EDGE,"E96.trimOffspring");Q77=makeQuery(id+"F1.imprint","IMPRINT",FACE,{"disambiguationData":[TD([[makeQuery(id+"F1.imprint","IMPRINT",EDGE,{"derivedFrom":subQ0}),-1.0]])]});}
            var Q78;
            {var subQ0=sQuery(id+"F1.wireOp",EDGE,"E139.trimOffspring");Q78=makeQuery(id+"F1.imprint","IMPRINT",FACE,{"disambiguationData":[TD([[makeQuery(id+"F1.imprint","IMPRINT",EDGE,{"derivedFrom":subQ0}),1.0]])]});}
            var Q79;
            {var subQ0=sQuery(id+"F1.wireOp",EDGE,"E84");var subQ1=sQuery(id+"F1.wireOp",EDGE,"E7.0");var subQ2=makeQuery(id+"F1.imprint","INTERSECT",VERTEX,{"derivedFrom":[subQ1,subQ0]});Q79=makeQuery(id+"F1.imprint","IMPRINT",FACE,{"disambiguationData":[TD([[makeQuery(id+"F1.imprint","IMPRINT",EDGE,{"disambiguationData":[TD([[subQ2,-1.0]])],"derivedFrom":subQ1}),1.0]])]});}
            var Q80;
            {var subQ0=sQuery(id+"F1.wireOp",EDGE,"E84");var subQ1=sQuery(id+"F1.wireOp",EDGE,"E30.0");var subQ2=makeQuery(id+"F1.imprint","INTERSECT",VERTEX,{"derivedFrom":[subQ1,subQ0]});Q80=makeQuery(id+"F1.imprint","IMPRINT",FACE,{"disambiguationData":[TD([[makeQuery(id+"F1.imprint","IMPRINT",EDGE,{"disambiguationData":[TD([[subQ2,-1.0]])],"derivedFrom":subQ1}),1.0]])]});}
            var Q81;
            {var subQ0=sQuery(id+"F1.wireOp",EDGE,"E125.trimOffspring");Q81=makeQuery(id+"F1.imprint","IMPRINT",FACE,{"disambiguationData":[TD([[makeQuery(id+"F1.imprint","IMPRINT",EDGE,{"derivedFrom":subQ0}),1.0]])]});}
            var Q82;
            {var subQ0=sQuery(id+"F1.wireOp",EDGE,"E124.trimOffspring");Q82=makeQuery(id+"F1.imprint","IMPRINT",FACE,{"disambiguationData":[TD([[makeQuery(id+"F1.imprint","IMPRINT",EDGE,{"derivedFrom":subQ0}),-1.0]])]});}
            var Q83;
            {var subQ0=sQuery(id+"F1.wireOp",EDGE,"E84");var subQ1=sQuery(id+"F1.wireOp",EDGE,"E27.0");var subQ2=makeQuery(id+"F1.imprint","INTERSECT",VERTEX,{"derivedFrom":[subQ1,subQ0]});Q83=makeQuery(id+"F1.imprint","IMPRINT",FACE,{"disambiguationData":[TD([[makeQuery(id+"F1.imprint","IMPRINT",EDGE,{"disambiguationData":[TD([[subQ2,-1.0]])],"derivedFrom":subQ1}),-1.0]])]});}
            var Q84;
            {var subQ0=sQuery(id+"F1.wireOp",EDGE,"E147.trimOffspring");Q84=makeQuery(id+"F1.imprint","IMPRINT",FACE,{"disambiguationData":[TD([[makeQuery(id+"F1.imprint","IMPRINT",EDGE,{"derivedFrom":subQ0}),1.0]])]});}
            var Q85;
            {var subQ0=sQuery(id+"F1.wireOp",EDGE,"E84");var subQ1=sQuery(id+"F1.wireOp",EDGE,"E37.0");var subQ2=makeQuery(id+"F1.imprint","INTERSECT",VERTEX,{"derivedFrom":[subQ1,subQ0]});Q85=makeQuery(id+"F1.imprint","IMPRINT",FACE,{"disambiguationData":[TD([[makeQuery(id+"F1.imprint","IMPRINT",EDGE,{"disambiguationData":[TD([[subQ2,-1.0]])],"derivedFrom":subQ1}),-1.0]])]});}
            var Q86;
            {var subQ0=sQuery(id+"F1.wireOp",EDGE,"E84");var subQ1=sQuery(id+"F1.wireOp",EDGE,"E32.0");var subQ2=makeQuery(id+"F1.imprint","INTERSECT",VERTEX,{"derivedFrom":[subQ1,subQ0]});Q86=makeQuery(id+"F1.imprint","IMPRINT",FACE,{"disambiguationData":[TD([[makeQuery(id+"F1.imprint","IMPRINT",EDGE,{"disambiguationData":[TD([[subQ2,-1.0]])],"derivedFrom":subQ1}),-1.0]])]});}
            var Q87;
            {var subQ0=sQuery(id+"F1.wireOp",EDGE,"E131");Q87=makeQuery(id+"F1.imprint","IMPRINT",FACE,{"disambiguationData":[TD([[makeQuery(id+"F1.imprint","IMPRINT",EDGE,{"derivedFrom":subQ0}),1.0]])]});}
            var Q88;
            {var subQ0=sQuery(id+"F1.wireOp",EDGE,"E84");var subQ1=sQuery(id+"F1.wireOp",EDGE,"E34.0");var subQ2=makeQuery(id+"F1.imprint","INTERSECT",VERTEX,{"derivedFrom":[subQ1,subQ0]});Q88=makeQuery(id+"F1.imprint","IMPRINT",FACE,{"disambiguationData":[TD([[makeQuery(id+"F1.imprint","IMPRINT",EDGE,{"disambiguationData":[TD([[subQ2,-1.0]])],"derivedFrom":subQ1}),-1.0]])]});}
            var Q89;
            {var subQ0=sQuery(id+"F1.wireOp",EDGE,"E84");var subQ1=sQuery(id+"F1.wireOp",EDGE,"E14.0");var subQ2=makeQuery(id+"F1.imprint","INTERSECT",VERTEX,{"derivedFrom":[subQ1,subQ0]});Q89=makeQuery(id+"F1.imprint","IMPRINT",FACE,{"disambiguationData":[TD([[makeQuery(id+"F1.imprint","IMPRINT",EDGE,{"disambiguationData":[TD([[subQ2,-1.0]])],"derivedFrom":subQ1}),1.0]])]});}
            var Q90;
            {var subQ0=sQuery(id+"F1.wireOp",EDGE,"E145.trimOffspring");Q90=makeQuery(id+"F1.imprint","IMPRINT",FACE,{"disambiguationData":[TD([[makeQuery(id+"F1.imprint","IMPRINT",EDGE,{"derivedFrom":subQ0}),1.0]])]});}
            var Q91;
            {var subQ0=sQuery(id+"F1.wireOp",EDGE,"E84");var subQ1=sQuery(id+"F1.wireOp",EDGE,"E44.0");var subQ2=makeQuery(id+"F1.imprint","INTERSECT",VERTEX,{"derivedFrom":[subQ1,subQ0]});Q91=makeQuery(id+"F1.imprint","IMPRINT",FACE,{"disambiguationData":[TD([[makeQuery(id+"F1.imprint","IMPRINT",EDGE,{"disambiguationData":[TD([[subQ2,-1.0]])],"derivedFrom":subQ1}),-1.0]])]});}
            var Q92;
            {var subQ0=sQuery(id+"F1.wireOp",EDGE,"E101.trimOffspring");Q92=makeQuery(id+"F1.imprint","IMPRINT",FACE,{"disambiguationData":[TD([[makeQuery(id+"F1.imprint","IMPRINT",EDGE,{"derivedFrom":subQ0}),-1.0]])]});}
            var Q93;
            {var subQ0=sQuery(id+"F1.wireOp",EDGE,"E84");var subQ1=sQuery(id+"F1.wireOp",EDGE,"E20.0");var subQ2=makeQuery(id+"F1.imprint","INTERSECT",VERTEX,{"derivedFrom":[subQ1,subQ0]});Q93=makeQuery(id+"F1.imprint","IMPRINT",FACE,{"disambiguationData":[TD([[makeQuery(id+"F1.imprint","IMPRINT",EDGE,{"disambiguationData":[TD([[subQ2,-1.0]])],"derivedFrom":subQ1}),-1.0]])]});}
            var Q94;
            {var subQ0=sQuery(id+"F1.wireOp",EDGE,"E89.trimOffspring");Q94=makeQuery(id+"F1.imprint","IMPRINT",FACE,{"disambiguationData":[TD([[makeQuery(id+"F1.imprint","IMPRINT",EDGE,{"derivedFrom":subQ0}),-1.0]])]});}
            var Q95;
            {var subQ0=sQuery(id+"F1.wireOp",EDGE,"E84");var subQ1=sQuery(id+"F1.wireOp",EDGE,"E36.0");var subQ2=makeQuery(id+"F1.imprint","INTERSECT",VERTEX,{"derivedFrom":[subQ1,subQ0]});Q95=makeQuery(id+"F1.imprint","IMPRINT",FACE,{"disambiguationData":[TD([[makeQuery(id+"F1.imprint","IMPRINT",EDGE,{"disambiguationData":[TD([[subQ2,-1.0]])],"derivedFrom":subQ1}),-1.0]])]});}
            var Q96;
            {var subQ0=sQuery(id+"F1.wireOp",EDGE,"E150.trimOffspring");Q96=makeQuery(id+"F1.imprint","IMPRINT",FACE,{"disambiguationData":[TD([[makeQuery(id+"F1.imprint","IMPRINT",EDGE,{"derivedFrom":subQ0}),1.0]])]});}
            var Q97;
            {var subQ0=sQuery(id+"F1.wireOp",EDGE,"E84");var subQ1=sQuery(id+"F1.wireOp",EDGE,"E34.0");var subQ2=makeQuery(id+"F1.imprint","INTERSECT",VERTEX,{"derivedFrom":[subQ1,subQ0]});Q97=makeQuery(id+"F1.imprint","IMPRINT",FACE,{"disambiguationData":[TD([[makeQuery(id+"F1.imprint","IMPRINT",EDGE,{"disambiguationData":[TD([[subQ2,-1.0]])],"derivedFrom":subQ1}),1.0]])]});}
            var Q98;
            {var subQ0=sQuery(id+"F1.wireOp",EDGE,"E103.trimOffspring");Q98=makeQuery(id+"F1.imprint","IMPRINT",FACE,{"disambiguationData":[TD([[makeQuery(id+"F1.imprint","IMPRINT",EDGE,{"derivedFrom":subQ0}),-1.0]])]});}
            var Q99;
            {var subQ0=sQuery(id+"F1.wireOp",EDGE,"E84");var subQ1=sQuery(id+"F1.wireOp",EDGE,"E16.0");var subQ2=makeQuery(id+"F1.imprint","INTERSECT",VERTEX,{"derivedFrom":[subQ1,subQ0]});Q99=makeQuery(id+"F1.imprint","IMPRINT",FACE,{"disambiguationData":[TD([[makeQuery(id+"F1.imprint","IMPRINT",EDGE,{"disambiguationData":[TD([[subQ2,-1.0]])],"derivedFrom":subQ1}),-1.0]])]});}
            var Q100;
            {var subQ0=sQuery(id+"F1.wireOp",EDGE,"E109.trimOffspring");Q100=makeQuery(id+"F1.imprint","IMPRINT",FACE,{"disambiguationData":[TD([[makeQuery(id+"F1.imprint","IMPRINT",EDGE,{"derivedFrom":subQ0}),-1.0]])]});}
            var Q101;
            {var subQ0=sQuery(id+"F1.wireOp",EDGE,"E155.trimOffspring");Q101=makeQuery(id+"F1.imprint","IMPRINT",FACE,{"disambiguationData":[TD([[makeQuery(id+"F1.imprint","IMPRINT",EDGE,{"derivedFrom":subQ0}),1.0]])]});}
            var Q102;
            {var subQ0=sQuery(id+"F1.wireOp",EDGE,"E90.trimOffspring");Q102=makeQuery(id+"F1.imprint","IMPRINT",FACE,{"disambiguationData":[TD([[makeQuery(id+"F1.imprint","IMPRINT",EDGE,{"derivedFrom":subQ0}),-1.0]])]});}
            var Q103;
            {var subQ0=sQuery(id+"F1.wireOp",EDGE,"E128.trimOffspring");Q103=makeQuery(id+"F1.imprint","IMPRINT",FACE,{"disambiguationData":[TD([[makeQuery(id+"F1.imprint","IMPRINT",EDGE,{"derivedFrom":subQ0}),1.0]])]});}
            var Q104;
            {var subQ0=sQuery(id+"F1.wireOp",EDGE,"E84");var subQ1=sQuery(id+"F1.wireOp",EDGE,"E23.0");var subQ2=makeQuery(id+"F1.imprint","INTERSECT",VERTEX,{"derivedFrom":[subQ1,subQ0]});Q104=makeQuery(id+"F1.imprint","IMPRINT",FACE,{"disambiguationData":[TD([[makeQuery(id+"F1.imprint","IMPRINT",EDGE,{"disambiguationData":[TD([[subQ2,-1.0]])],"derivedFrom":subQ1}),-1.0]])]});}
            var Q105;
            {var subQ0=sQuery(id+"F1.wireOp",EDGE,"E84");var subQ1=sQuery(id+"F1.wireOp",EDGE,"E42.0");var subQ2=makeQuery(id+"F1.imprint","INTERSECT",VERTEX,{"derivedFrom":[subQ1,subQ0]});Q105=makeQuery(id+"F1.imprint","IMPRINT",FACE,{"disambiguationData":[TD([[makeQuery(id+"F1.imprint","IMPRINT",EDGE,{"disambiguationData":[TD([[subQ2,-1.0]])],"derivedFrom":subQ1}),1.0]])]});}
            var Q106;
            {var subQ0=sQuery(id+"F1.wireOp",EDGE,"E108.trimOffspring");Q106=makeQuery(id+"F1.imprint","IMPRINT",FACE,{"disambiguationData":[TD([[makeQuery(id+"F1.imprint","IMPRINT",EDGE,{"derivedFrom":subQ0}),-1.0]])]});}
            var Q107;
            {var subQ0=sQuery(id+"F1.wireOp",EDGE,"E84");var subQ1=sQuery(id+"F1.wireOp",EDGE,"E29.0");var subQ2=makeQuery(id+"F1.imprint","INTERSECT",VERTEX,{"derivedFrom":[subQ1,subQ0]});Q107=makeQuery(id+"F1.imprint","IMPRINT",FACE,{"disambiguationData":[TD([[makeQuery(id+"F1.imprint","IMPRINT",EDGE,{"disambiguationData":[TD([[subQ2,-1.0]])],"derivedFrom":subQ1}),1.0]])]});}
            var Q108;
            {var subQ0=sQuery(id+"F1.wireOp",EDGE,"E110.trimOffspring");Q108=makeQuery(id+"F1.imprint","IMPRINT",FACE,{"disambiguationData":[TD([[makeQuery(id+"F1.imprint","IMPRINT",EDGE,{"derivedFrom":subQ0}),-1.0]])]});}
            var Q109;
            {var subQ0=sQuery(id+"F1.wireOp",EDGE,"E159");Q109=makeQuery(id+"F1.imprint","IMPRINT",FACE,{"disambiguationData":[TD([[makeQuery(id+"F1.imprint","IMPRINT",EDGE,{"derivedFrom":subQ0}),1.0]])]});}
            var Q110;
            {var subQ0=sQuery(id+"F1.wireOp",EDGE,"E119.trimOffspring");Q110=makeQuery(id+"F1.imprint","IMPRINT",FACE,{"disambiguationData":[TD([[makeQuery(id+"F1.imprint","IMPRINT",EDGE,{"derivedFrom":subQ0}),-1.0]])]});}
            var Q111;
            {var subQ0=sQuery(id+"F1.wireOp",EDGE,"E84");var subQ1=sQuery(id+"F1.wireOp",EDGE,"E24.0");var subQ2=makeQuery(id+"F1.imprint","INTERSECT",VERTEX,{"derivedFrom":[subQ1,subQ0]});Q111=makeQuery(id+"F1.imprint","IMPRINT",FACE,{"disambiguationData":[TD([[makeQuery(id+"F1.imprint","IMPRINT",EDGE,{"disambiguationData":[TD([[subQ2,-1.0]])],"derivedFrom":subQ1}),-1.0]])]});}
            var Q112;
            {var subQ0=sQuery(id+"F1.wireOp",EDGE,"E97.trimOffspring");Q112=makeQuery(id+"F1.imprint","IMPRINT",FACE,{"disambiguationData":[TD([[makeQuery(id+"F1.imprint","IMPRINT",EDGE,{"derivedFrom":subQ0}),-1.0]])]});}
            var Q113;
            {var subQ0=sQuery(id+"F1.wireOp",EDGE,"E84");var subQ1=sQuery(id+"F1.wireOp",EDGE,"E23.0");var subQ2=makeQuery(id+"F1.imprint","INTERSECT",VERTEX,{"derivedFrom":[subQ1,subQ0]});Q113=makeQuery(id+"F1.imprint","IMPRINT",FACE,{"disambiguationData":[TD([[makeQuery(id+"F1.imprint","IMPRINT",EDGE,{"disambiguationData":[TD([[subQ2,-1.0]])],"derivedFrom":subQ1}),1.0]])]});}
            var Q114;
            {var subQ0=sQuery(id+"F1.wireOp",EDGE,"E132");Q114=makeQuery(id+"F1.imprint","IMPRINT",FACE,{"disambiguationData":[TD([[makeQuery(id+"F1.imprint","IMPRINT",EDGE,{"derivedFrom":subQ0}),1.0]])]});}
            var Q115;
            {var subQ0=sQuery(id+"F1.wireOp",EDGE,"E84");var subQ1=sQuery(id+"F1.wireOp",EDGE,"E8.0");var subQ2=makeQuery(id+"F1.imprint","INTERSECT",VERTEX,{"derivedFrom":[subQ1,subQ0]});Q115=makeQuery(id+"F1.imprint","IMPRINT",FACE,{"disambiguationData":[TD([[makeQuery(id+"F1.imprint","IMPRINT",EDGE,{"disambiguationData":[TD([[subQ2,-1.0]])],"derivedFrom":subQ1}),1.0]])]});}
            var Q116;
            {var subQ0=sQuery(id+"F1.wireOp",EDGE,"E84");var subQ1=sQuery(id+"F1.wireOp",EDGE,"E16.0");var subQ2=makeQuery(id+"F1.imprint","INTERSECT",VERTEX,{"derivedFrom":[subQ1,subQ0]});Q116=makeQuery(id+"F1.imprint","IMPRINT",FACE,{"disambiguationData":[TD([[makeQuery(id+"F1.imprint","IMPRINT",EDGE,{"disambiguationData":[TD([[subQ2,-1.0]])],"derivedFrom":subQ1}),1.0]])]});}
            var Q117;
            {var subQ0=sQuery(id+"F1.wireOp",EDGE,"E84");var subQ1=sQuery(id+"F1.wireOp",EDGE,"E15.0");var subQ2=makeQuery(id+"F1.imprint","INTERSECT",VERTEX,{"derivedFrom":[subQ1,subQ0]});Q117=makeQuery(id+"F1.imprint","IMPRINT",FACE,{"disambiguationData":[TD([[makeQuery(id+"F1.imprint","IMPRINT",EDGE,{"disambiguationData":[TD([[subQ2,-1.0]])],"derivedFrom":subQ1}),1.0]])]});}
            var Q118;
            {var subQ0=sQuery(id+"F1.wireOp",EDGE,"E84");var subQ1=sQuery(id+"F1.wireOp",EDGE,"E41.0");var subQ2=makeQuery(id+"F1.imprint","INTERSECT",VERTEX,{"derivedFrom":[subQ1,subQ0]});Q118=makeQuery(id+"F1.imprint","IMPRINT",FACE,{"disambiguationData":[TD([[makeQuery(id+"F1.imprint","IMPRINT",EDGE,{"disambiguationData":[TD([[subQ2,-1.0]])],"derivedFrom":subQ1}),-1.0]])]});}
            var Q119;
            {var subQ0=sQuery(id+"F1.wireOp",EDGE,"E157.trimOffspring");Q119=makeQuery(id+"F1.imprint","IMPRINT",FACE,{"disambiguationData":[TD([[makeQuery(id+"F1.imprint","IMPRINT",EDGE,{"derivedFrom":subQ0}),1.0]])]});}
            var Q120;
            {var subQ0=sQuery(id+"F1.wireOp",EDGE,"E84");var subQ1=sQuery(id+"F1.wireOp",EDGE,"E6.0");var subQ2=makeQuery(id+"F1.imprint","INTERSECT",VERTEX,{"derivedFrom":[subQ1,subQ0]});Q120=makeQuery(id+"F1.imprint","IMPRINT",FACE,{"disambiguationData":[TD([[makeQuery(id+"F1.imprint","IMPRINT",EDGE,{"disambiguationData":[TD([[subQ2,-1.0]])],"derivedFrom":subQ1}),1.0]])]});}
            var Q121;
            {var subQ0=sQuery(id+"F1.wireOp",EDGE,"E104.trimOffspring");Q121=makeQuery(id+"F1.imprint","IMPRINT",FACE,{"disambiguationData":[TD([[makeQuery(id+"F1.imprint","IMPRINT",EDGE,{"derivedFrom":subQ0}),-1.0]])]});}
            var Q122;
            {var subQ0=sQuery(id+"F1.wireOp",EDGE,"E94.trimOffspring");Q122=makeQuery(id+"F1.imprint","IMPRINT",FACE,{"disambiguationData":[TD([[makeQuery(id+"F1.imprint","IMPRINT",EDGE,{"derivedFrom":subQ0}),-1.0]])]});}
            var Q123;
            {var subQ0=sQuery(id+"F1.wireOp",EDGE,"E84");var subQ1=sQuery(id+"F1.wireOp",EDGE,"E11.0");var subQ2=makeQuery(id+"F1.imprint","INTERSECT",VERTEX,{"derivedFrom":[subQ1,subQ0]});Q123=makeQuery(id+"F1.imprint","IMPRINT",FACE,{"disambiguationData":[TD([[makeQuery(id+"F1.imprint","IMPRINT",EDGE,{"disambiguationData":[TD([[subQ2,-1.0]])],"derivedFrom":subQ1}),-1.0]])]});}
            var Q124;
            {var subQ0=sQuery(id+"F1.wireOp",EDGE,"E84");var subQ1=sQuery(id+"F1.wireOp",EDGE,"E38.0");var subQ2=makeQuery(id+"F1.imprint","INTERSECT",VERTEX,{"derivedFrom":[subQ1,subQ0]});Q124=makeQuery(id+"F1.imprint","IMPRINT",FACE,{"disambiguationData":[TD([[makeQuery(id+"F1.imprint","IMPRINT",EDGE,{"disambiguationData":[TD([[subQ2,-1.0]])],"derivedFrom":subQ1}),-1.0]])]});}
            var Q125;
            {var subQ0=sQuery(id+"F1.wireOp",EDGE,"E84");var subQ1=sQuery(id+"F1.wireOp",EDGE,"E10.0");var subQ2=makeQuery(id+"F1.imprint","INTERSECT",VERTEX,{"derivedFrom":[subQ1,subQ0]});Q125=makeQuery(id+"F1.imprint","IMPRINT",FACE,{"disambiguationData":[TD([[makeQuery(id+"F1.imprint","IMPRINT",EDGE,{"disambiguationData":[TD([[subQ2,-1.0]])],"derivedFrom":subQ1}),1.0]])]});}
            var Q126;
            {var subQ0=sQuery(id+"F1.wireOp",EDGE,"E111.trimOffspring");Q126=makeQuery(id+"F1.imprint","IMPRINT",FACE,{"disambiguationData":[TD([[makeQuery(id+"F1.imprint","IMPRINT",EDGE,{"derivedFrom":subQ0}),-1.0]])]});}
            var Q127;
            {var subQ0=sQuery(id+"F1.wireOp",EDGE,"E144.trimOffspring");Q127=makeQuery(id+"F1.imprint","IMPRINT",FACE,{"disambiguationData":[TD([[makeQuery(id+"F1.imprint","IMPRINT",EDGE,{"derivedFrom":subQ0}),1.0]])]});}
            var Q128;
            {var subQ0=sQuery(id+"F1.wireOp",EDGE,"E135.trimOffspring");Q128=makeQuery(id+"F1.imprint","IMPRINT",FACE,{"disambiguationData":[TD([[makeQuery(id+"F1.imprint","IMPRINT",EDGE,{"derivedFrom":subQ0}),1.0]])]});}
            var Q129;
            {var subQ0=sQuery(id+"F1.wireOp",EDGE,"E84");var subQ1=sQuery(id+"F1.wireOp",EDGE,"E13.0");var subQ2=makeQuery(id+"F1.imprint","INTERSECT",VERTEX,{"derivedFrom":[subQ1,subQ0]});Q129=makeQuery(id+"F1.imprint","IMPRINT",FACE,{"disambiguationData":[TD([[makeQuery(id+"F1.imprint","IMPRINT",EDGE,{"disambiguationData":[TD([[subQ2,-1.0]])],"derivedFrom":subQ1}),1.0]])]});}
            var Q130;
            {var subQ0=sQuery(id+"F1.wireOp",EDGE,"E84");var subQ1=sQuery(id+"F1.wireOp",EDGE,"E25.0");var subQ2=makeQuery(id+"F1.imprint","INTERSECT",VERTEX,{"derivedFrom":[subQ1,subQ0]});Q130=makeQuery(id+"F1.imprint","IMPRINT",FACE,{"disambiguationData":[TD([[makeQuery(id+"F1.imprint","IMPRINT",EDGE,{"disambiguationData":[TD([[subQ2,-1.0]])],"derivedFrom":subQ1}),1.0]])]});}
            var Q131;
            {var subQ0=sQuery(id+"F1.wireOp",EDGE,"E162");Q131=makeQuery(id+"F1.imprint","IMPRINT",FACE,{"disambiguationData":[TD([[makeQuery(id+"F1.imprint","IMPRINT",EDGE,{"derivedFrom":subQ0}),1.0]])]});}
            var Q132;
            {var subQ0=sQuery(id+"F1.wireOp",EDGE,"E137");Q132=makeQuery(id+"F1.imprint","IMPRINT",FACE,{"disambiguationData":[TD([[makeQuery(id+"F1.imprint","IMPRINT",EDGE,{"derivedFrom":subQ0}),1.0]])]});}
            var Q133;
            {var subQ0=sQuery(id+"F1.wireOp",EDGE,"E116.trimOffspring");Q133=makeQuery(id+"F1.imprint","IMPRINT",FACE,{"disambiguationData":[TD([[makeQuery(id+"F1.imprint","IMPRINT",EDGE,{"derivedFrom":subQ0}),-1.0]])]});}
            var Q134;
            {var subQ0=sQuery(id+"F1.wireOp",EDGE,"E126.trimOffspring");Q134=makeQuery(id+"F1.imprint","IMPRINT",FACE,{"disambiguationData":[TD([[makeQuery(id+"F1.imprint","IMPRINT",EDGE,{"derivedFrom":subQ0}),1.0]])]});}
            var Q135;
            {var subQ0=sQuery(id+"F1.wireOp",EDGE,"E84");var subQ1=sQuery(id+"F1.wireOp",EDGE,"E9.0");var subQ2=makeQuery(id+"F1.imprint","INTERSECT",VERTEX,{"derivedFrom":[subQ1,subQ0]});Q135=makeQuery(id+"F1.imprint","IMPRINT",FACE,{"disambiguationData":[TD([[makeQuery(id+"F1.imprint","IMPRINT",EDGE,{"disambiguationData":[TD([[subQ2,-1.0]])],"derivedFrom":subQ1}),1.0]])]});}
            var Q136;
            {var subQ0=sQuery(id+"F1.wireOp",EDGE,"E84");var subQ1=sQuery(id+"F1.wireOp",EDGE,"E40.0");var subQ2=makeQuery(id+"F1.imprint","INTERSECT",VERTEX,{"derivedFrom":[subQ1,subQ0]});Q136=makeQuery(id+"F1.imprint","IMPRINT",FACE,{"disambiguationData":[TD([[makeQuery(id+"F1.imprint","IMPRINT",EDGE,{"disambiguationData":[TD([[subQ2,-1.0]])],"derivedFrom":subQ1}),-1.0]])]});}
            var Q137;
            {var subQ0=sQuery(id+"F1.wireOp",EDGE,"E149.trimOffspring");Q137=makeQuery(id+"F1.imprint","IMPRINT",FACE,{"disambiguationData":[TD([[makeQuery(id+"F1.imprint","IMPRINT",EDGE,{"derivedFrom":subQ0}),1.0]])]});}
            var Q138;
            {var subQ0=sQuery(id+"F1.wireOp",EDGE,"E84");var subQ1=sQuery(id+"F1.wireOp",EDGE,"E25.0");var subQ2=makeQuery(id+"F1.imprint","INTERSECT",VERTEX,{"derivedFrom":[subQ1,subQ0]});Q138=makeQuery(id+"F1.imprint","IMPRINT",FACE,{"disambiguationData":[TD([[makeQuery(id+"F1.imprint","IMPRINT",EDGE,{"disambiguationData":[TD([[subQ2,-1.0]])],"derivedFrom":subQ1}),-1.0]])]});}
            var Q139;
            {var subQ0=sQuery(id+"F1.wireOp",EDGE,"E84");var subQ1=sQuery(id+"F1.wireOp",EDGE,"E41.0");var subQ2=makeQuery(id+"F1.imprint","INTERSECT",VERTEX,{"derivedFrom":[subQ1,subQ0]});Q139=makeQuery(id+"F1.imprint","IMPRINT",FACE,{"disambiguationData":[TD([[makeQuery(id+"F1.imprint","IMPRINT",EDGE,{"disambiguationData":[TD([[subQ2,-1.0]])],"derivedFrom":subQ1}),1.0]])]});}
            var Q140;
            {var subQ0=sQuery(id+"F1.wireOp",EDGE,"E84");var subQ1=sQuery(id+"F1.wireOp",EDGE,"E45.0");var subQ2=makeQuery(id+"F1.imprint","INTERSECT",VERTEX,{"derivedFrom":[subQ1,subQ0]});Q140=makeQuery(id+"F1.imprint","IMPRINT",FACE,{"disambiguationData":[TD([[makeQuery(id+"F1.imprint","IMPRINT",EDGE,{"disambiguationData":[TD([[subQ2,-1.0]])],"derivedFrom":subQ1}),-1.0]])]});}
            var Q141;
            {var subQ0=sQuery(id+"F1.wireOp",EDGE,"E98.trimOffspring");Q141=makeQuery(id+"F1.imprint","IMPRINT",FACE,{"disambiguationData":[TD([[makeQuery(id+"F1.imprint","IMPRINT",EDGE,{"derivedFrom":subQ0}),-1.0]])]});}
            var Q142;
            {var subQ0=sQuery(id+"F1.wireOp",EDGE,"E163");Q142=makeQuery(id+"F1.imprint","IMPRINT",FACE,{"disambiguationData":[TD([[makeQuery(id+"F1.imprint","IMPRINT",EDGE,{"derivedFrom":subQ0}),1.0]])]});}
            var Q143;
            {var subQ0=sQuery(id+"F1.wireOp",EDGE,"E153");Q143=makeQuery(id+"F1.imprint","IMPRINT",FACE,{"disambiguationData":[TD([[makeQuery(id+"F1.imprint","IMPRINT",EDGE,{"derivedFrom":subQ0}),1.0]])]});}
            var Q144;
            {var subQ0=sQuery(id+"F1.wireOp",EDGE,"E113.trimOffspring");Q144=makeQuery(id+"F1.imprint","IMPRINT",FACE,{"disambiguationData":[TD([[makeQuery(id+"F1.imprint","IMPRINT",EDGE,{"derivedFrom":subQ0}),-1.0]])]});}
            var Q145;
            {var subQ0=sQuery(id+"F1.wireOp",EDGE,"E84");var subQ1=sQuery(id+"F1.wireOp",EDGE,"E22.0");var subQ2=makeQuery(id+"F1.imprint","INTERSECT",VERTEX,{"derivedFrom":[subQ1,subQ0]});Q145=makeQuery(id+"F1.imprint","IMPRINT",FACE,{"disambiguationData":[TD([[makeQuery(id+"F1.imprint","IMPRINT",EDGE,{"disambiguationData":[TD([[subQ2,-1.0]])],"derivedFrom":subQ1}),1.0]])]});}
            var Q146;
            {var subQ0=sQuery(id+"F1.wireOp",EDGE,"E84");var subQ1=sQuery(id+"F1.wireOp",EDGE,"E39.0");var subQ2=makeQuery(id+"F1.imprint","INTERSECT",VERTEX,{"derivedFrom":[subQ1,subQ0]});Q146=makeQuery(id+"F1.imprint","IMPRINT",FACE,{"disambiguationData":[TD([[makeQuery(id+"F1.imprint","IMPRINT",EDGE,{"disambiguationData":[TD([[subQ2,-1.0]])],"derivedFrom":subQ1}),-1.0]])]});}
            var Q147;
            {var subQ0=sQuery(id+"F1.wireOp",EDGE,"E84");var subQ1=sQuery(id+"F1.wireOp",EDGE,"E33.0");var subQ2=makeQuery(id+"F1.imprint","INTERSECT",VERTEX,{"derivedFrom":[subQ1,subQ0]});Q147=makeQuery(id+"F1.imprint","IMPRINT",FACE,{"disambiguationData":[TD([[makeQuery(id+"F1.imprint","IMPRINT",EDGE,{"disambiguationData":[TD([[subQ2,-1.0]])],"derivedFrom":subQ1}),1.0]])]});}
            var Q148;
            {var subQ0=sQuery(id+"F1.wireOp",EDGE,"E84");var subQ1=sQuery(id+"F1.wireOp",EDGE,"E5.0");var subQ2=makeQuery(id+"F1.imprint","INTERSECT",VERTEX,{"derivedFrom":[subQ1,subQ0]});Q148=makeQuery(id+"F1.imprint","IMPRINT",FACE,{"disambiguationData":[TD([[makeQuery(id+"F1.imprint","IMPRINT",EDGE,{"disambiguationData":[TD([[subQ2,-1.0]])],"derivedFrom":subQ1}),1.0]])]});}
            var Q149;
            {var subQ0=sQuery(id+"F1.wireOp",EDGE,"E160");Q149=makeQuery(id+"F1.imprint","IMPRINT",FACE,{"disambiguationData":[TD([[makeQuery(id+"F1.imprint","IMPRINT",EDGE,{"derivedFrom":subQ0}),1.0]])]});}
            var Q150;
            {var subQ0=sQuery(id+"F1.wireOp",EDGE,"E84");var subQ1=sQuery(id+"F1.wireOp",EDGE,"E20.0");var subQ2=makeQuery(id+"F1.imprint","INTERSECT",VERTEX,{"derivedFrom":[subQ1,subQ0]});Q150=makeQuery(id+"F1.imprint","IMPRINT",FACE,{"disambiguationData":[TD([[makeQuery(id+"F1.imprint","IMPRINT",EDGE,{"disambiguationData":[TD([[subQ2,-1.0]])],"derivedFrom":subQ1}),1.0]])]});}
            var Q151;
            {var subQ0=sQuery(id+"F1.wireOp",EDGE,"E114.trimOffspring");Q151=makeQuery(id+"F1.imprint","IMPRINT",FACE,{"disambiguationData":[TD([[makeQuery(id+"F1.imprint","IMPRINT",EDGE,{"derivedFrom":subQ0}),-1.0]])]});}
            var Q152;
            {var subQ0=sQuery(id+"F1.wireOp",EDGE,"E136.trimOffspring");Q152=makeQuery(id+"F1.imprint","IMPRINT",FACE,{"disambiguationData":[TD([[makeQuery(id+"F1.imprint","IMPRINT",EDGE,{"derivedFrom":subQ0}),1.0]])]});}
            var Q153;
            {var subQ0=sQuery(id+"F1.wireOp",EDGE,"E84");var subQ1=sQuery(id+"F1.wireOp",EDGE,"E4");var subQ2=makeQuery(id+"F1.imprint","INTERSECT",VERTEX,{"derivedFrom":[subQ1,subQ0]});Q153=makeQuery(id+"F1.imprint","IMPRINT",FACE,{"disambiguationData":[TD([[makeQuery(id+"F1.imprint","IMPRINT",EDGE,{"disambiguationData":[TD([[subQ2,1.0]])],"derivedFrom":subQ1}),1.0]])]});}
            var Q154;
            {var subQ0=sQuery(id+"F1.wireOp",EDGE,"E84");var subQ1=sQuery(id+"F1.wireOp",EDGE,"E2");var subQ2=makeQuery(id+"F1.imprint","INTERSECT",VERTEX,{"derivedFrom":[subQ1,subQ0]});Q154=makeQuery(id+"F1.imprint","IMPRINT",FACE,{"disambiguationData":[TD([[makeQuery(id+"F1.imprint","IMPRINT",EDGE,{"disambiguationData":[TD([[subQ2,-1.0]])],"derivedFrom":subQ1}),1.0]])]});}
            var Q155;
            {var subQ0=sQuery(id+"F1.wireOp",EDGE,"E3");Q155=makeQuery(id+"F1.imprint","IMPRINT",FACE,{"disambiguationData":[TD([[makeQuery(id+"F1.imprint","IMPRINT",EDGE,{"derivedFrom":subQ0}),1.0]])]});}
            var Q156;
            {var subQ0=sQuery(id+"F1.wireOp",EDGE,"E86.trimOffspring");Q156=makeQuery(id+"F1.imprint","IMPRINT",FACE,{"disambiguationData":[TD([[makeQuery(id+"F1.imprint","IMPRINT",EDGE,{"derivedFrom":subQ0}),-1.0]])]});}
            var Q157;
            {var subQ0=sQuery(id+"F1.wireOp",EDGE,"E156.trimOffspring");Q157=makeQuery(id+"F1.imprint","IMPRINT",FACE,{"disambiguationData":[TD([[makeQuery(id+"F1.imprint","IMPRINT",EDGE,{"derivedFrom":subQ0}),1.0]])]});}
            var Q158;
            {var subQ0=sQuery(id+"F1.wireOp",EDGE,"E1");Q158=makeQuery(id+"F1.imprint","IMPRINT",FACE,{"disambiguationData":[TD([[makeQuery(id+"F1.imprint","IMPRINT",EDGE,{"derivedFrom":subQ0}),-1.0]])]});}
            extrude(context, id + "F2", {"entities" : qUnion([Q0, Q1, Q2, Q3, Q4, Q5, Q6, Q7, Q8, Q9, Q10, Q11, Q12, Q13, Q14, Q15, Q16, Q17, Q18, Q19, Q20, Q21, Q22, Q23, Q24, Q25, Q26, Q27, Q28, Q29, Q30, Q31, Q32, Q33, Q34, Q35, Q36, Q37, Q38, Q39, Q40, Q41, Q42, Q43, Q44, Q45, Q46, Q47, Q48, Q49, Q50, Q51, Q52, Q53, Q54, Q55, Q56, Q57, Q58, Q59, Q60, Q61, Q62, Q63, Q64, Q65, Q66, Q67, Q68, Q69, Q70, Q71, Q72, Q73, Q74, Q75, Q76, Q77, Q78, Q79, Q80, Q81, Q82, Q83, Q84, Q85, Q86, Q87, Q88, Q89, Q90, Q91, Q92, Q93, Q94, Q95, Q96, Q97, Q98, Q99, Q100, Q101, Q102, Q103, Q104, Q105, Q106, Q107, Q108, Q109, Q110, Q111, Q112, Q113, Q114, Q115, Q116, Q117, Q118, Q119, Q120, Q121, Q122, Q123, Q124, Q125, Q126, Q127, Q128, Q129, Q130, Q131, Q132, Q133, Q134, Q135, Q136, Q137, Q138, Q139, Q140, Q141, Q142, Q143, Q144, Q145, Q146, Q147, Q148, Q149, Q150, Q151, Q152, Q153, Q154, Q155, Q156, Q157, Q158]), "depth" : 3416 * mm, "offsetDistance" : 25 * mm});
        }
        {
            var Q0;
            Q0=makeQuery(id+"F2.opExtrude","SWEPT_FACE",FACE,{"disambiguationData":[OSD([sQuery(id+"F1.wireOp",EDGE,"E2")])]});
            var sketch = newSketch(context, id + "F3", { "sketchPlane" : qUnion([Q0])});
            skPoint(sketch, "E164", {"position": v(-4201, 3416) * mm});
            skLineSegment(sketch, "E165", {"start": v(-4201, 3416) * mm, "end": v(-4201, 3416) * mm});
            skLineSegment(sketch, "E166", {"start": v(-4201, 3916) * mm, "end": v(-4201, 3416) * mm});
            skLineSegment(sketch, "E167", {"start": v(-4201, 3416) * mm, "end": v(-3851, 3416) * mm});
            skLineSegment(sketch, "E168", {"start": v(-3851, 3416) * mm, "end": v(-3851, 3916) * mm});
            skLineSegment(sketch, "E169", {"start": v(-3851, 3916) * mm, "end": v(-4201, 3916) * mm});
            skSolve(sketch);
        }
        {
            var Q0;
            {var subQ0=sQuery(id+"F1.wireOp",EDGE,"E151.trimOffspring");var subQ1=sQuery(id+"F1.wireOp",EDGE,"E83.0");var subQ2=sQuery(id+"F1.wireOp",EDGE,"E85");var subQ4=sQuery(id+"F1.wireOp",EDGE,"E154");var subQ5=sQuery(id+"F1.wireOp",EDGE,"E82.0");var subQ7=sQuery(id+"F1.wireOp",EDGE,"E155.trimOffspring");var subQ8=sQuery(id+"F1.wireOp",EDGE,"E81.0");var subQ10=sQuery(id+"F1.wireOp",EDGE,"E150.trimOffspring");var subQ11=sQuery(id+"F1.wireOp",EDGE,"E80.0");var subQ13=sQuery(id+"F1.wireOp",EDGE,"E153");var subQ14=sQuery(id+"F1.wireOp",EDGE,"E79.0");var subQ16=sQuery(id+"F1.wireOp",EDGE,"E152");var subQ17=sQuery(id+"F1.wireOp",EDGE,"E78.0");var subQ19=sQuery(id+"F1.wireOp",EDGE,"E149.trimOffspring");var subQ20=sQuery(id+"F1.wireOp",EDGE,"E77.0");var subQ22=sQuery(id+"F1.wireOp",EDGE,"E148.trimOffspring");var subQ23=sQuery(id+"F1.wireOp",EDGE,"E76.0");var subQ25=sQuery(id+"F1.wireOp",EDGE,"E147.trimOffspring");var subQ26=sQuery(id+"F1.wireOp",EDGE,"E75.0");var subQ28=sQuery(id+"F1.wireOp",EDGE,"E145.trimOffspring");var subQ29=sQuery(id+"F1.wireOp",EDGE,"E74.0");var subQ31=sQuery(id+"F1.wireOp",EDGE,"E146.trimOffspring");var subQ32=sQuery(id+"F1.wireOp",EDGE,"E73.0");var subQ34=sQuery(id+"F1.wireOp",EDGE,"E144.trimOffspring");var subQ35=sQuery(id+"F1.wireOp",EDGE,"E72.0");var subQ37=sQuery(id+"F1.wireOp",EDGE,"E163");var subQ38=sQuery(id+"F1.wireOp",EDGE,"E71.0");var subQ40=sQuery(id+"F1.wireOp",EDGE,"E143.trimOffspring");var subQ41=sQuery(id+"F1.wireOp",EDGE,"E70.0");var subQ43=sQuery(id+"F1.wireOp",EDGE,"E142.trimOffspring");var subQ44=sQuery(id+"F1.wireOp",EDGE,"E69.0");var subQ46=sQuery(id+"F1.wireOp",EDGE,"E139.trimOffspring");var subQ47=sQuery(id+"F1.wireOp",EDGE,"E68.0");var subQ49=sQuery(id+"F1.wireOp",EDGE,"E140.trimOffspring");var subQ50=sQuery(id+"F1.wireOp",EDGE,"E67.0");var subQ52=sQuery(id+"F1.wireOp",EDGE,"E138.trimOffspring");var subQ53=sQuery(id+"F1.wireOp",EDGE,"E66.0");var subQ55=sQuery(id+"F1.wireOp",EDGE,"E141");var subQ56=sQuery(id+"F1.wireOp",EDGE,"E65.0");var subQ58=sQuery(id+"F1.wireOp",EDGE,"E134.trimOffspring");var subQ59=sQuery(id+"F1.wireOp",EDGE,"E64.0");var subQ61=sQuery(id+"F1.wireOp",EDGE,"E137");var subQ62=sQuery(id+"F1.wireOp",EDGE,"E63.0");var subQ64=sQuery(id+"F1.wireOp",EDGE,"E135.trimOffspring");var subQ65=sQuery(id+"F1.wireOp",EDGE,"E62.0");var subQ67=sQuery(id+"F1.wireOp",EDGE,"E19.0");var subQ69=sQuery(id+"F1.wireOp",EDGE,"E58.0");var subQ71=sQuery(id+"F1.wireOp",EDGE,"E159");var subQ72=sQuery(id+"F1.wireOp",EDGE,"E9.0");var subQ74=sQuery(id+"F1.wireOp",EDGE,"E136.trimOffspring");var subQ75=sQuery(id+"F1.wireOp",EDGE,"E61.0");var subQ77=sQuery(id+"F1.wireOp",EDGE,"E162");var subQ78=sQuery(id+"F1.wireOp",EDGE,"E17.0");var subQ80=sQuery(id+"F1.wireOp",EDGE,"E56.0");var subQ82=sQuery(id+"F1.wireOp",EDGE,"E158.trimOffspring");var subQ83=sQuery(id+"F1.wireOp",EDGE,"E8.0");var subQ85=sQuery(id+"F1.wireOp",EDGE,"E133.trimOffspring");var subQ86=sQuery(id+"F1.wireOp",EDGE,"E60.0");var subQ88=sQuery(id+"F1.wireOp",EDGE,"E160");var subQ89=sQuery(id+"F1.wireOp",EDGE,"E15.0");var subQ91=sQuery(id+"F1.wireOp",EDGE,"E54.0");var subQ93=sQuery(id+"F1.wireOp",EDGE,"E125.trimOffspring");var subQ94=sQuery(id+"F1.wireOp",EDGE,"E7.0");var subQ96=sQuery(id+"F1.wireOp",EDGE,"E161");var subQ97=sQuery(id+"F1.wireOp",EDGE,"E59.0");var subQ99=sQuery(id+"F1.wireOp",EDGE,"E13.0");var subQ101=sQuery(id+"F1.wireOp",EDGE,"E52.0");var subQ103=sQuery(id+"F1.wireOp",EDGE,"E6.0");var subQ105=sQuery(id+"F1.wireOp",EDGE,"E129.trimOffspring");var subQ106=sQuery(id+"F1.wireOp",EDGE,"E156.trimOffspring");var subQ107=sQuery(id+"F1.wireOp",EDGE,"E11.0");var subQ109=sQuery(id+"F1.wireOp",EDGE,"E50.0");var subQ111=sQuery(id+"F1.wireOp",EDGE,"E5.0");var subQ112=sQuery(id+"F1.wireOp",EDGE,"E3");var subQ114=sQuery(id+"F1.wireOp",EDGE,"E132");var subQ115=sQuery(id+"F1.wireOp",EDGE,"E57.0");var subQ117=sQuery(id+"F1.wireOp",EDGE,"E48.0");var subQ119=sQuery(id+"F1.wireOp",EDGE,"E4");var subQ120=sQuery(id+"F1.wireOp",EDGE,"E130.trimOffspring");var subQ121=sQuery(id+"F1.wireOp",EDGE,"E46.0");var subQ123=sQuery(id+"F1.wireOp",EDGE,"E2");var subQ124=sQuery(id+"F1.wireOp",EDGE,"E128.trimOffspring");var subQ125=sQuery(id+"F1.wireOp",EDGE,"E55.0");var subQ127=sQuery(id+"F1.wireOp",EDGE,"E131");var subQ128=sQuery(id+"F1.wireOp",EDGE,"E157.trimOffspring");var subQ129=sQuery(id+"F1.wireOp",EDGE,"E51.0");var subQ131=sQuery(id+"F1.wireOp",EDGE,"E126.trimOffspring");var subQ132=sQuery(id+"F1.wireOp",EDGE,"E49.0");var subQ134=sQuery(id+"F1.wireOp",EDGE,"E24.0");var subQ136=sQuery(id+"F1.wireOp",EDGE,"E23.0");var subQ138=sQuery(id+"F1.wireOp",EDGE,"E22.0");var subQ140=sQuery(id+"F1.wireOp",EDGE,"E44.0");var subQ142=sQuery(id+"F1.wireOp",EDGE,"E20.0");var subQ144=sQuery(id+"F1.wireOp",EDGE,"E42.0");var subQ146=sQuery(id+"F1.wireOp",EDGE,"E40.0");var subQ148=sQuery(id+"F1.wireOp",EDGE,"E18.0");var subQ150=sQuery(id+"F1.wireOp",EDGE,"E38.0");var subQ152=sQuery(id+"F1.wireOp",EDGE,"E36.0");var subQ154=sQuery(id+"F1.wireOp",EDGE,"E16.0");var subQ156=sQuery(id+"F1.wireOp",EDGE,"E34.0");var subQ158=sQuery(id+"F1.wireOp",EDGE,"E14.0");var subQ160=sQuery(id+"F1.wireOp",EDGE,"E30.0");var subQ162=sQuery(id+"F1.wireOp",EDGE,"E127.trimOffspring");var subQ163=sQuery(id+"F1.wireOp",EDGE,"E28.0");var subQ165=sQuery(id+"F1.wireOp",EDGE,"E12.0");var subQ167=sQuery(id+"F1.wireOp",EDGE,"E26.0");var subQ169=sQuery(id+"F1.wireOp",EDGE,"E32.0");var subQ171=sQuery(id+"F1.wireOp",EDGE,"E53.0");var subQ173=sQuery(id+"F1.wireOp",EDGE,"E47.0");var subQ175=sQuery(id+"F1.wireOp",EDGE,"E10.0");var subQ177=sQuery(id+"F1.wireOp",EDGE,"E25.0");var subQ179=sQuery(id+"F1.wireOp",EDGE,"E27.0");var subQ181=sQuery(id+"F1.wireOp",EDGE,"E29.0");var subQ183=sQuery(id+"F1.wireOp",EDGE,"E31.0");var subQ185=sQuery(id+"F1.wireOp",EDGE,"E33.0");var subQ187=sQuery(id+"F1.wireOp",EDGE,"E35.0");var subQ189=sQuery(id+"F1.wireOp",EDGE,"E37.0");var subQ191=sQuery(id+"F1.wireOp",EDGE,"E39.0");var subQ193=sQuery(id+"F1.wireOp",EDGE,"E41.0");var subQ195=sQuery(id+"F1.wireOp",EDGE,"E43.0");var subQ197=sQuery(id+"F1.wireOp",EDGE,"E45.0");Q0=makeQuery(id+"FzMqNVo3a2xKz4z_1.boolean.opBoolean","SPLIT",FACE,{"disambiguationData":[TD([makeQuery(id+"F2.opExtrude","SWEPT_FACE",FACE,{"disambiguationData":[OSD([subQ112])]})])],"derivedFrom":makeQuery(id+"F2.opExtrude","CAP_FACE",FACE,{"disambiguationData":[OSD([sQuery(id+"F1.wireOp",EDGE,"E1"),subQ123,subQ112,subQ119,subQ111,subQ103,subQ94,subQ83,subQ72,subQ175,subQ107,subQ165,subQ99,subQ158,subQ89,subQ154,subQ78,subQ148,subQ67,subQ142,subQ138,subQ136,subQ134,subQ177,subQ167,subQ179,subQ163,subQ181,subQ160,subQ183,subQ169,subQ185,subQ156,subQ187,subQ152,subQ189,subQ150,subQ191,subQ146,subQ193,subQ144,subQ195,subQ140,subQ197,subQ121,subQ173,subQ117,subQ132,subQ109,subQ129,subQ101,subQ171,subQ91,subQ125,subQ80,subQ115,subQ69,subQ97,subQ86,subQ75,subQ65,subQ62,subQ59,subQ56,subQ53,subQ50,subQ47,subQ44,subQ41,subQ38,subQ35,subQ32,subQ29,subQ26,subQ23,subQ20,subQ17,subQ14,subQ11,subQ8,subQ5,subQ1,sQuery(id+"F1.wireOp",EDGE,"E84"),subQ2,sQuery(id+"F1.wireOp",EDGE,"E86.trimOffspring"),sQuery(id+"F1.wireOp",EDGE,"E87.trimOffspring"),sQuery(id+"F1.wireOp",EDGE,"E88.trimOffspring"),sQuery(id+"F1.wireOp",EDGE,"E89.trimOffspring"),sQuery(id+"F1.wireOp",EDGE,"E90.trimOffspring"),sQuery(id+"F1.wireOp",EDGE,"E91.trimOffspring"),sQuery(id+"F1.wireOp",EDGE,"E92.trimOffspring"),sQuery(id+"F1.wireOp",EDGE,"E93.trimOffspring"),sQuery(id+"F1.wireOp",EDGE,"E94.trimOffspring"),sQuery(id+"F1.wireOp",EDGE,"E95.trimOffspring"),sQuery(id+"F1.wireOp",EDGE,"E96.trimOffspring"),sQuery(id+"F1.wireOp",EDGE,"E97.trimOffspring"),sQuery(id+"F1.wireOp",EDGE,"E98.trimOffspring"),sQuery(id+"F1.wireOp",EDGE,"E99.trimOffspring"),sQuery(id+"F1.wireOp",EDGE,"E100.trimOffspring"),sQuery(id+"F1.wireOp",EDGE,"E101.trimOffspring"),sQuery(id+"F1.wireOp",EDGE,"E102.trimOffspring"),sQuery(id+"F1.wireOp",EDGE,"E103.trimOffspring"),sQuery(id+"F1.wireOp",EDGE,"E104.trimOffspring"),sQuery(id+"F1.wireOp",EDGE,"E105.trimOffspring"),sQuery(id+"F1.wireOp",EDGE,"E106.trimOffspring"),sQuery(id+"F1.wireOp",EDGE,"E107.trimOffspring"),sQuery(id+"F1.wireOp",EDGE,"E108.trimOffspring"),sQuery(id+"F1.wireOp",EDGE,"E109.trimOffspring"),sQuery(id+"F1.wireOp",EDGE,"E110.trimOffspring"),sQuery(id+"F1.wireOp",EDGE,"E111.trimOffspring"),sQuery(id+"F1.wireOp",EDGE,"E112.trimOffspring"),sQuery(id+"F1.wireOp",EDGE,"E113.trimOffspring"),sQuery(id+"F1.wireOp",EDGE,"E114.trimOffspring"),sQuery(id+"F1.wireOp",EDGE,"E115.trimOffspring"),sQuery(id+"F1.wireOp",EDGE,"E116.trimOffspring"),sQuery(id+"F1.wireOp",EDGE,"E117.trimOffspring"),sQuery(id+"F1.wireOp",EDGE,"E118.trimOffspring"),sQuery(id+"F1.wireOp",EDGE,"E119.trimOffspring"),sQuery(id+"F1.wireOp",EDGE,"E120.trimOffspring"),sQuery(id+"F1.wireOp",EDGE,"E121.trimOffspring"),sQuery(id+"F1.wireOp",EDGE,"E122.trimOffspring"),sQuery(id+"F1.wireOp",EDGE,"E123.trimOffspring"),sQuery(id+"F1.wireOp",EDGE,"E124.trimOffspring"),subQ93,subQ131,subQ162,subQ124,subQ105,subQ120,subQ127,subQ114,subQ85,subQ58,subQ64,subQ74,subQ61,subQ52,subQ46,subQ49,subQ55,subQ43,subQ40,subQ34,subQ28,subQ31,subQ25,subQ22,subQ19,subQ10,subQ0,subQ16,subQ13,subQ4,subQ7,subQ106,subQ128,subQ82,subQ71,subQ88,subQ96,subQ77,subQ37])],"isStart":false})});}
            var sketch = newSketch(context, id + "F4", { "sketchPlane" : qUnion([Q0])});
            skLineSegment(sketch, "E170", {"start": v(-17701.46, 3651) * mm, "end": v(-15201.46, 3651) * mm});
            skLineSegment(sketch, "E171", {"start": v(-15201.46, 3651) * mm, "end": v(-15201.46, 3301) * mm});
            skLineSegment(sketch, "E172", {"start": v(-15201.46, 3301) * mm, "end": v(-17701.46, 3301) * mm});
            skLineSegment(sketch, "E173", {"start": v(-17701.46, 3301) * mm, "end": v(-17701.46, 3651) * mm});
            skSolve(sketch);
        }
        {
            var Q0;
            {var subQ0=sQuery(id+"F1.wireOp",EDGE,"E151.trimOffspring");var subQ1=sQuery(id+"F1.wireOp",EDGE,"E83.0");var subQ2=sQuery(id+"F1.wireOp",EDGE,"E85");var subQ4=sQuery(id+"F1.wireOp",EDGE,"E154");var subQ5=sQuery(id+"F1.wireOp",EDGE,"E82.0");var subQ7=sQuery(id+"F1.wireOp",EDGE,"E155.trimOffspring");var subQ8=sQuery(id+"F1.wireOp",EDGE,"E81.0");var subQ10=sQuery(id+"F1.wireOp",EDGE,"E150.trimOffspring");var subQ11=sQuery(id+"F1.wireOp",EDGE,"E80.0");var subQ13=sQuery(id+"F1.wireOp",EDGE,"E153");var subQ14=sQuery(id+"F1.wireOp",EDGE,"E79.0");var subQ16=sQuery(id+"F1.wireOp",EDGE,"E152");var subQ17=sQuery(id+"F1.wireOp",EDGE,"E78.0");var subQ19=sQuery(id+"F1.wireOp",EDGE,"E149.trimOffspring");var subQ20=sQuery(id+"F1.wireOp",EDGE,"E77.0");var subQ22=sQuery(id+"F1.wireOp",EDGE,"E148.trimOffspring");var subQ23=sQuery(id+"F1.wireOp",EDGE,"E76.0");var subQ25=sQuery(id+"F1.wireOp",EDGE,"E147.trimOffspring");var subQ26=sQuery(id+"F1.wireOp",EDGE,"E75.0");var subQ28=sQuery(id+"F1.wireOp",EDGE,"E145.trimOffspring");var subQ29=sQuery(id+"F1.wireOp",EDGE,"E74.0");var subQ31=sQuery(id+"F1.wireOp",EDGE,"E146.trimOffspring");var subQ32=sQuery(id+"F1.wireOp",EDGE,"E73.0");var subQ34=sQuery(id+"F1.wireOp",EDGE,"E144.trimOffspring");var subQ35=sQuery(id+"F1.wireOp",EDGE,"E72.0");var subQ37=sQuery(id+"F1.wireOp",EDGE,"E163");var subQ38=sQuery(id+"F1.wireOp",EDGE,"E71.0");var subQ40=sQuery(id+"F1.wireOp",EDGE,"E143.trimOffspring");var subQ41=sQuery(id+"F1.wireOp",EDGE,"E70.0");var subQ43=sQuery(id+"F1.wireOp",EDGE,"E142.trimOffspring");var subQ44=sQuery(id+"F1.wireOp",EDGE,"E69.0");var subQ46=sQuery(id+"F1.wireOp",EDGE,"E139.trimOffspring");var subQ47=sQuery(id+"F1.wireOp",EDGE,"E68.0");var subQ49=sQuery(id+"F1.wireOp",EDGE,"E140.trimOffspring");var subQ50=sQuery(id+"F1.wireOp",EDGE,"E67.0");var subQ52=sQuery(id+"F1.wireOp",EDGE,"E138.trimOffspring");var subQ53=sQuery(id+"F1.wireOp",EDGE,"E66.0");var subQ55=sQuery(id+"F1.wireOp",EDGE,"E141");var subQ56=sQuery(id+"F1.wireOp",EDGE,"E65.0");var subQ58=sQuery(id+"F1.wireOp",EDGE,"E134.trimOffspring");var subQ59=sQuery(id+"F1.wireOp",EDGE,"E64.0");var subQ61=sQuery(id+"F1.wireOp",EDGE,"E137");var subQ62=sQuery(id+"F1.wireOp",EDGE,"E63.0");var subQ64=sQuery(id+"F1.wireOp",EDGE,"E135.trimOffspring");var subQ65=sQuery(id+"F1.wireOp",EDGE,"E62.0");var subQ67=sQuery(id+"F1.wireOp",EDGE,"E19.0");var subQ69=sQuery(id+"F1.wireOp",EDGE,"E58.0");var subQ71=sQuery(id+"F1.wireOp",EDGE,"E159");var subQ72=sQuery(id+"F1.wireOp",EDGE,"E9.0");var subQ74=sQuery(id+"F1.wireOp",EDGE,"E136.trimOffspring");var subQ75=sQuery(id+"F1.wireOp",EDGE,"E61.0");var subQ77=sQuery(id+"F1.wireOp",EDGE,"E162");var subQ78=sQuery(id+"F1.wireOp",EDGE,"E17.0");var subQ80=sQuery(id+"F1.wireOp",EDGE,"E56.0");var subQ82=sQuery(id+"F1.wireOp",EDGE,"E158.trimOffspring");var subQ83=sQuery(id+"F1.wireOp",EDGE,"E8.0");var subQ85=sQuery(id+"F1.wireOp",EDGE,"E133.trimOffspring");var subQ86=sQuery(id+"F1.wireOp",EDGE,"E60.0");var subQ88=sQuery(id+"F1.wireOp",EDGE,"E160");var subQ89=sQuery(id+"F1.wireOp",EDGE,"E15.0");var subQ91=sQuery(id+"F1.wireOp",EDGE,"E54.0");var subQ93=sQuery(id+"F1.wireOp",EDGE,"E125.trimOffspring");var subQ94=sQuery(id+"F1.wireOp",EDGE,"E7.0");var subQ96=sQuery(id+"F1.wireOp",EDGE,"E161");var subQ97=sQuery(id+"F1.wireOp",EDGE,"E59.0");var subQ99=sQuery(id+"F1.wireOp",EDGE,"E13.0");var subQ101=sQuery(id+"F1.wireOp",EDGE,"E52.0");var subQ103=sQuery(id+"F1.wireOp",EDGE,"E6.0");var subQ105=sQuery(id+"F1.wireOp",EDGE,"E129.trimOffspring");var subQ106=sQuery(id+"F1.wireOp",EDGE,"E156.trimOffspring");var subQ107=sQuery(id+"F1.wireOp",EDGE,"E11.0");var subQ109=sQuery(id+"F1.wireOp",EDGE,"E50.0");var subQ111=sQuery(id+"F1.wireOp",EDGE,"E5.0");var subQ112=sQuery(id+"F1.wireOp",EDGE,"E3");var subQ114=sQuery(id+"F1.wireOp",EDGE,"E132");var subQ115=sQuery(id+"F1.wireOp",EDGE,"E57.0");var subQ117=sQuery(id+"F1.wireOp",EDGE,"E48.0");var subQ119=sQuery(id+"F1.wireOp",EDGE,"E4");var subQ120=sQuery(id+"F1.wireOp",EDGE,"E130.trimOffspring");var subQ121=sQuery(id+"F1.wireOp",EDGE,"E46.0");var subQ123=sQuery(id+"F1.wireOp",EDGE,"E2");var subQ124=sQuery(id+"F1.wireOp",EDGE,"E128.trimOffspring");var subQ125=sQuery(id+"F1.wireOp",EDGE,"E55.0");var subQ127=sQuery(id+"F1.wireOp",EDGE,"E131");var subQ128=sQuery(id+"F1.wireOp",EDGE,"E157.trimOffspring");var subQ129=sQuery(id+"F1.wireOp",EDGE,"E51.0");var subQ131=sQuery(id+"F1.wireOp",EDGE,"E126.trimOffspring");var subQ132=sQuery(id+"F1.wireOp",EDGE,"E49.0");var subQ134=sQuery(id+"F1.wireOp",EDGE,"E24.0");var subQ136=sQuery(id+"F1.wireOp",EDGE,"E23.0");var subQ138=sQuery(id+"F1.wireOp",EDGE,"E22.0");var subQ140=sQuery(id+"F1.wireOp",EDGE,"E44.0");var subQ142=sQuery(id+"F1.wireOp",EDGE,"E20.0");var subQ144=sQuery(id+"F1.wireOp",EDGE,"E42.0");var subQ146=sQuery(id+"F1.wireOp",EDGE,"E40.0");var subQ148=sQuery(id+"F1.wireOp",EDGE,"E18.0");var subQ150=sQuery(id+"F1.wireOp",EDGE,"E38.0");var subQ152=sQuery(id+"F1.wireOp",EDGE,"E36.0");var subQ154=sQuery(id+"F1.wireOp",EDGE,"E16.0");var subQ156=sQuery(id+"F1.wireOp",EDGE,"E34.0");var subQ158=sQuery(id+"F1.wireOp",EDGE,"E14.0");var subQ160=sQuery(id+"F1.wireOp",EDGE,"E30.0");var subQ162=sQuery(id+"F1.wireOp",EDGE,"E127.trimOffspring");var subQ163=sQuery(id+"F1.wireOp",EDGE,"E28.0");var subQ165=sQuery(id+"F1.wireOp",EDGE,"E12.0");var subQ167=sQuery(id+"F1.wireOp",EDGE,"E26.0");var subQ169=sQuery(id+"F1.wireOp",EDGE,"E32.0");var subQ171=sQuery(id+"F1.wireOp",EDGE,"E53.0");var subQ173=sQuery(id+"F1.wireOp",EDGE,"E47.0");var subQ175=sQuery(id+"F1.wireOp",EDGE,"E10.0");var subQ177=sQuery(id+"F1.wireOp",EDGE,"E25.0");var subQ179=sQuery(id+"F1.wireOp",EDGE,"E27.0");var subQ181=sQuery(id+"F1.wireOp",EDGE,"E29.0");var subQ183=sQuery(id+"F1.wireOp",EDGE,"E31.0");var subQ185=sQuery(id+"F1.wireOp",EDGE,"E33.0");var subQ187=sQuery(id+"F1.wireOp",EDGE,"E35.0");var subQ189=sQuery(id+"F1.wireOp",EDGE,"E37.0");var subQ191=sQuery(id+"F1.wireOp",EDGE,"E39.0");var subQ193=sQuery(id+"F1.wireOp",EDGE,"E41.0");var subQ195=sQuery(id+"F1.wireOp",EDGE,"E43.0");var subQ197=sQuery(id+"F1.wireOp",EDGE,"E45.0");Q0=makeQuery(id+"FzMqNVo3a2xKz4z_1.boolean.opBoolean","SPLIT",FACE,{"disambiguationData":[TD([makeQuery(id+"F2.opExtrude","SWEPT_FACE",FACE,{"disambiguationData":[OSD([subQ112])]})])],"derivedFrom":makeQuery(id+"F2.opExtrude","CAP_FACE",FACE,{"disambiguationData":[OSD([sQuery(id+"F1.wireOp",EDGE,"E1"),subQ123,subQ112,subQ119,subQ111,subQ103,subQ94,subQ83,subQ72,subQ175,subQ107,subQ165,subQ99,subQ158,subQ89,subQ154,subQ78,subQ148,subQ67,subQ142,subQ138,subQ136,subQ134,subQ177,subQ167,subQ179,subQ163,subQ181,subQ160,subQ183,subQ169,subQ185,subQ156,subQ187,subQ152,subQ189,subQ150,subQ191,subQ146,subQ193,subQ144,subQ195,subQ140,subQ197,subQ121,subQ173,subQ117,subQ132,subQ109,subQ129,subQ101,subQ171,subQ91,subQ125,subQ80,subQ115,subQ69,subQ97,subQ86,subQ75,subQ65,subQ62,subQ59,subQ56,subQ53,subQ50,subQ47,subQ44,subQ41,subQ38,subQ35,subQ32,subQ29,subQ26,subQ23,subQ20,subQ17,subQ14,subQ11,subQ8,subQ5,subQ1,sQuery(id+"F1.wireOp",EDGE,"E84"),subQ2,sQuery(id+"F1.wireOp",EDGE,"E86.trimOffspring"),sQuery(id+"F1.wireOp",EDGE,"E87.trimOffspring"),sQuery(id+"F1.wireOp",EDGE,"E88.trimOffspring"),sQuery(id+"F1.wireOp",EDGE,"E89.trimOffspring"),sQuery(id+"F1.wireOp",EDGE,"E90.trimOffspring"),sQuery(id+"F1.wireOp",EDGE,"E91.trimOffspring"),sQuery(id+"F1.wireOp",EDGE,"E92.trimOffspring"),sQuery(id+"F1.wireOp",EDGE,"E93.trimOffspring"),sQuery(id+"F1.wireOp",EDGE,"E94.trimOffspring"),sQuery(id+"F1.wireOp",EDGE,"E95.trimOffspring"),sQuery(id+"F1.wireOp",EDGE,"E96.trimOffspring"),sQuery(id+"F1.wireOp",EDGE,"E97.trimOffspring"),sQuery(id+"F1.wireOp",EDGE,"E98.trimOffspring"),sQuery(id+"F1.wireOp",EDGE,"E99.trimOffspring"),sQuery(id+"F1.wireOp",EDGE,"E100.trimOffspring"),sQuery(id+"F1.wireOp",EDGE,"E101.trimOffspring"),sQuery(id+"F1.wireOp",EDGE,"E102.trimOffspring"),sQuery(id+"F1.wireOp",EDGE,"E103.trimOffspring"),sQuery(id+"F1.wireOp",EDGE,"E104.trimOffspring"),sQuery(id+"F1.wireOp",EDGE,"E105.trimOffspring"),sQuery(id+"F1.wireOp",EDGE,"E106.trimOffspring"),sQuery(id+"F1.wireOp",EDGE,"E107.trimOffspring"),sQuery(id+"F1.wireOp",EDGE,"E108.trimOffspring"),sQuery(id+"F1.wireOp",EDGE,"E109.trimOffspring"),sQuery(id+"F1.wireOp",EDGE,"E110.trimOffspring"),sQuery(id+"F1.wireOp",EDGE,"E111.trimOffspring"),sQuery(id+"F1.wireOp",EDGE,"E112.trimOffspring"),sQuery(id+"F1.wireOp",EDGE,"E113.trimOffspring"),sQuery(id+"F1.wireOp",EDGE,"E114.trimOffspring"),sQuery(id+"F1.wireOp",EDGE,"E115.trimOffspring"),sQuery(id+"F1.wireOp",EDGE,"E116.trimOffspring"),sQuery(id+"F1.wireOp",EDGE,"E117.trimOffspring"),sQuery(id+"F1.wireOp",EDGE,"E118.trimOffspring"),sQuery(id+"F1.wireOp",EDGE,"E119.trimOffspring"),sQuery(id+"F1.wireOp",EDGE,"E120.trimOffspring"),sQuery(id+"F1.wireOp",EDGE,"E121.trimOffspring"),sQuery(id+"F1.wireOp",EDGE,"E122.trimOffspring"),sQuery(id+"F1.wireOp",EDGE,"E123.trimOffspring"),sQuery(id+"F1.wireOp",EDGE,"E124.trimOffspring"),subQ93,subQ131,subQ162,subQ124,subQ105,subQ120,subQ127,subQ114,subQ85,subQ58,subQ64,subQ74,subQ61,subQ52,subQ46,subQ49,subQ55,subQ43,subQ40,subQ34,subQ28,subQ31,subQ25,subQ22,subQ19,subQ10,subQ0,subQ16,subQ13,subQ4,subQ7,subQ106,subQ128,subQ82,subQ71,subQ88,subQ96,subQ77,subQ37])],"isStart":false})});}
            var sketch = newSketch(context, id + "F5", { "sketchPlane" : qUnion([Q0])});
            skLineSegment(sketch, "E174", {"start": v(-17701.46, 3201) * mm, "end": v(-17701.46, 2851) * mm});
            skLineSegment(sketch, "E175", {"start": v(-17701.46, 2851) * mm, "end": v(-16785.46, 2851) * mm});
            skLineSegment(sketch, "E176", {"start": v(-16785.46, 2851) * mm, "end": v(-16785.46, 3201) * mm});
            skLineSegment(sketch, "E177", {"start": v(-16785.46, 3201) * mm, "end": v(-17701.46, 3201) * mm});
            skLineSegment(sketch, "E178.MirrorCS", {"start": v(-16117.46, 2851) * mm, "end": v(-16117.46, 3201) * mm});
            skLineSegment(sketch, "E179.MirrorCS", {"start": v(-16117.46, 3201) * mm, "end": v(-15201.46, 3201) * mm});
            skLineSegment(sketch, "E180.MirrorCS", {"start": v(-15201.46, 2851) * mm, "end": v(-16117.46, 2851) * mm});
            skLineSegment(sketch, "E181.MirrorCS", {"start": v(-15201.46, 3201) * mm, "end": v(-15201.46, 2851) * mm});
            skSolve(sketch);
        }
        {
            var Q0;
            Q0=makeQuery(id+"F5.imprint","IMPRINT",FACE,{"disambiguationData":[TD([[makeQuery(id+"F5.imprint","IMPRINT",EDGE,{"derivedFrom":sQuery(id+"F5.wireOp",EDGE,"E174")}),1.0]])]});
            var Q1;
            Q1=makeQuery(id+"F5.imprint","IMPRINT",FACE,{"disambiguationData":[TD([[makeQuery(id+"F5.imprint","IMPRINT",EDGE,{"derivedFrom":sQuery(id+"F5.wireOp",EDGE,"E178.MirrorCS")}),-1.0]])]});
            extrude(context, id + "F6", {"entities" : qUnion([Q0, Q1]), "operationType" : NewBodyOperationType.ADD, "depth" : 1044 * mm, "offsetDistance" : 25 * mm});
        }
        {
            var Q0;
            Q0=makeQuery(id+"F4.imprint","IMPRINT",FACE,{"disambiguationData":[TD([[makeQuery(id+"F4.imprint","IMPRINT",EDGE,{"derivedFrom":sQuery(id+"F4.wireOp",EDGE,"E170")}),-1.0]])]});
            extrude(context, id + "F7", {"entities" : qUnion([Q0]), "operationType" : NewBodyOperationType.ADD, "depth" : 800 * mm, "offsetDistance" : 25 * mm});
        }
        {
            var Q0;
            Q0=makeQuery(id+"F7RHQ93fltytKVB_1.boolean.opBoolean","MERGE",FACE,{"derivedFrom":[makeQuery(id+"F2.opExtrude","SWEPT_FACE",FACE,{"disambiguationData":[OSD([sQuery(id+"F1.wireOp",EDGE,"E2")])]}),makeQuery(id+"F7RHQ93fltytKVB_1.opExtrude","CAP_FACE",FACE,{"disambiguationData":[OSD([sQuery(id+"F3.wireOp",EDGE,"E166"),sQuery(id+"F3.wireOp",EDGE,"E167"),sQuery(id+"F3.wireOp",EDGE,"E168"),sQuery(id+"F3.wireOp",EDGE,"E169")])],"isStart":true})]});
            var sketch = newSketch(context, id + "F8", { "sketchPlane" : qUnion([Q0])});
            skLineSegment(sketch, "E182", {"start": v(-4551, 3416) * mm, "end": v(-4551, 3916) * mm});
            skLineSegment(sketch, "E183", {"start": v(-4551, 3916) * mm, "end": v(-4901, 3916) * mm});
            skLineSegment(sketch, "E184", {"start": v(-4901, 3916) * mm, "end": v(-4901, 3416) * mm});
            skLineSegment(sketch, "E185", {"start": v(-4901, 3416) * mm, "end": v(-4551, 3416) * mm});
            skSolve(sketch);
        }
        {
            var Q0;
            Q0=makeQuery(id+"F8.imprint","IMPRINT",FACE,{"disambiguationData":[TD([[makeQuery(id+"F8.imprint","IMPRINT",EDGE,{"derivedFrom":sQuery(id+"F8.wireOp",EDGE,"E182")}),1.0]])]});
            extrude(context, id + "F9", {"entities" : qUnion([Q0]), "operationType" : NewBodyOperationType.ADD, "oppositeDirection" : true, "depth" : 11725 * mm, "offsetDistance" : 25 * mm});
        }
        {
            var Q0;
            Q0=makeQuery(id+"F6.opExtrude","SWEPT_FACE",FACE,{"disambiguationData":[OSD([sQuery(id+"F5.wireOp",EDGE,"E181.MirrorCS")])]});
            var sketch = newSketch(context, id + "F10", { "sketchPlane" : qUnion([Q0])});
            skLineSegment(sketch, "E186", {"start": v(2851, 4460) * mm, "end": v(3201, 4460) * mm});
            skLineSegment(sketch, "E187", {"start": v(3201, 4460) * mm, "end": v(3201, 3960) * mm});
            skLineSegment(sketch, "E188", {"start": v(3201, 3960) * mm, "end": v(2851, 3960) * mm});
            skLineSegment(sketch, "E189", {"start": v(2851, 3960) * mm, "end": v(2851, 4460) * mm});
            skSolve(sketch);
        }
        {
            var Q0;
            Q0=makeQuery(id+"F10.imprint","IMPRINT",FACE,{"disambiguationData":[TD([[makeQuery(id+"F10.imprint","IMPRINT",EDGE,{"derivedFrom":sQuery(id+"F10.wireOp",EDGE,"E186")}),1.0]])]});
            extrude(context, id + "F11", {"entities" : qUnion([Q0]), "operationType" : NewBodyOperationType.ADD, "depth" : 500 * mm, "offsetDistance" : 25 * mm});
        }
        {
            var Q0;
            Q0=makeQuery(id+"F11.boolean.opBoolean","MERGE",FACE,{"derivedFrom":[makeQuery(id+"F6.opExtrude","CAP_FACE",FACE,{"disambiguationData":[OSD([sQuery(id+"F5.wireOp",EDGE,"E178.MirrorCS"),sQuery(id+"F5.wireOp",EDGE,"E179.MirrorCS"),sQuery(id+"F5.wireOp",EDGE,"E180.MirrorCS"),sQuery(id+"F5.wireOp",EDGE,"E181.MirrorCS")])],"isStart":false}),makeQuery(id+"F11.opExtrude","SWEPT_FACE",FACE,{"disambiguationData":[OSD([sQuery(id+"F10.wireOp",EDGE,"E186")])]})]});
            var sketch = newSketch(context, id + "F12", { "sketchPlane" : qUnion([Q0])});
            skLineSegment(sketch, "E190", {"start": v(-14701.46, 3201) * mm, "end": v(-14151.46, 3201) * mm});
            skLineSegment(sketch, "E191", {"start": v(-13976.46, 3376) * mm, "end": v(-13976.46, 4326) * mm});
            skLineSegment(sketch, "E192", {"start": v(-14701.46, 3201) * mm, "end": v(-14701.46, 2851) * mm});
            skLineSegment(sketch, "E193", {"start": v(-14701.46, 2851) * mm, "end": v(-14151.46, 2851) * mm});
            skPoint(sketch, "E194.visualSharp", {"position": v(-13626.46, 2851) * mm});
            skArc(sketch, "E194.filletArc", {"start": v(-14151.46, 2851) * mm, "mid": v(-13780.23, 3004.77) * mm, "end": v(-13626.46, 3376) * mm});
            skPoint(sketch, "E195.visualSharp", {"position": v(-13976.46, 3201) * mm});
            skArc(sketch, "E195.filletArc", {"start": v(-14151.46, 3201) * mm, "mid": v(-14027.72, 3252.26) * mm, "end": v(-13976.46, 3376) * mm});
            skLineSegment(sketch, "E196", {"start": v(-14051.46, 4551) * mm, "end": v(-13551.46, 4551) * mm});
            skLineSegment(sketch, "E197", {"start": v(-13626.46, 4326) * mm, "end": v(-13551.46, 4551) * mm});
            skLineSegment(sketch, "E198", {"start": v(-13976.46, 4326) * mm, "end": v(-14051.46, 4551) * mm});
            skLineSegment(sketch, "E199", {"start": v(-13626.46, 3376) * mm, "end": v(-13626.46, 4326) * mm});
            skLineSegment(sketch, "E200", {"start": v(-16201.46, 4135.96) * mm, "end": v(-16201.46, 1909.35) * mm});
            skLineSegment(sketch, "E201.MirrorCS", {"start": v(-14701.46, 2851) * mm, "end": v(-15251.46, 2851) * mm});
            skLineSegment(sketch, "E202.MirrorCS", {"start": v(-17701.46, 2851) * mm, "end": v(-18251.46, 2851) * mm});
            skLineSegment(sketch, "E203.MirrorCS", {"start": v(-17701.46, 3201) * mm, "end": v(-17701.46, 2851) * mm});
            skLineSegment(sketch, "E204.MirrorCS", {"start": v(-17701.46, 3201) * mm, "end": v(-18251.46, 3201) * mm});
            skArc(sketch, "E205.MirrorCS", {"start": v(-18251.46, 3201) * mm, "mid": v(-18375.2, 3252.26) * mm, "end": v(-18426.46, 3376) * mm});
            skArc(sketch, "E206.MirrorCS", {"start": v(-18251.46, 2851) * mm, "mid": v(-18622.7, 3004.77) * mm, "end": v(-18776.46, 3376) * mm});
            skLineSegment(sketch, "E207.MirrorCS", {"start": v(-18426.46, 3376) * mm, "end": v(-18426.46, 4326) * mm});
            skLineSegment(sketch, "E208.MirrorCS", {"start": v(-18776.46, 3376) * mm, "end": v(-18776.46, 4326) * mm});
            skLineSegment(sketch, "E209.MirrorCS", {"start": v(-18776.46, 4326) * mm, "end": v(-18851.46, 4551) * mm});
            skLineSegment(sketch, "E210.MirrorCS", {"start": v(-18426.46, 4326) * mm, "end": v(-18351.46, 4551) * mm});
            skLineSegment(sketch, "E211.MirrorCS", {"start": v(-18351.46, 4551) * mm, "end": v(-18851.46, 4551) * mm});
            skSolve(sketch);
        }
        {
            var Q0;
            {var subQ0=sQuery(id+"F1.wireOp",EDGE,"E151.trimOffspring");var subQ1=sQuery(id+"F1.wireOp",EDGE,"E83.0");var subQ2=sQuery(id+"F1.wireOp",EDGE,"E85");var subQ4=sQuery(id+"F1.wireOp",EDGE,"E154");var subQ5=sQuery(id+"F1.wireOp",EDGE,"E82.0");var subQ7=sQuery(id+"F1.wireOp",EDGE,"E155.trimOffspring");var subQ8=sQuery(id+"F1.wireOp",EDGE,"E81.0");var subQ10=sQuery(id+"F1.wireOp",EDGE,"E150.trimOffspring");var subQ11=sQuery(id+"F1.wireOp",EDGE,"E80.0");var subQ13=sQuery(id+"F1.wireOp",EDGE,"E153");var subQ14=sQuery(id+"F1.wireOp",EDGE,"E79.0");var subQ16=sQuery(id+"F1.wireOp",EDGE,"E152");var subQ17=sQuery(id+"F1.wireOp",EDGE,"E78.0");var subQ19=sQuery(id+"F1.wireOp",EDGE,"E149.trimOffspring");var subQ20=sQuery(id+"F1.wireOp",EDGE,"E77.0");var subQ22=sQuery(id+"F1.wireOp",EDGE,"E148.trimOffspring");var subQ23=sQuery(id+"F1.wireOp",EDGE,"E76.0");var subQ25=sQuery(id+"F1.wireOp",EDGE,"E147.trimOffspring");var subQ26=sQuery(id+"F1.wireOp",EDGE,"E75.0");var subQ28=sQuery(id+"F1.wireOp",EDGE,"E145.trimOffspring");var subQ29=sQuery(id+"F1.wireOp",EDGE,"E74.0");var subQ31=sQuery(id+"F1.wireOp",EDGE,"E146.trimOffspring");var subQ32=sQuery(id+"F1.wireOp",EDGE,"E73.0");var subQ34=sQuery(id+"F1.wireOp",EDGE,"E144.trimOffspring");var subQ35=sQuery(id+"F1.wireOp",EDGE,"E72.0");var subQ37=sQuery(id+"F1.wireOp",EDGE,"E163");var subQ38=sQuery(id+"F1.wireOp",EDGE,"E71.0");var subQ40=sQuery(id+"F1.wireOp",EDGE,"E143.trimOffspring");var subQ41=sQuery(id+"F1.wireOp",EDGE,"E70.0");var subQ43=sQuery(id+"F1.wireOp",EDGE,"E142.trimOffspring");var subQ44=sQuery(id+"F1.wireOp",EDGE,"E69.0");var subQ46=sQuery(id+"F1.wireOp",EDGE,"E139.trimOffspring");var subQ47=sQuery(id+"F1.wireOp",EDGE,"E68.0");var subQ49=sQuery(id+"F1.wireOp",EDGE,"E140.trimOffspring");var subQ50=sQuery(id+"F1.wireOp",EDGE,"E67.0");var subQ52=sQuery(id+"F1.wireOp",EDGE,"E138.trimOffspring");var subQ53=sQuery(id+"F1.wireOp",EDGE,"E66.0");var subQ55=sQuery(id+"F1.wireOp",EDGE,"E141");var subQ56=sQuery(id+"F1.wireOp",EDGE,"E65.0");var subQ58=sQuery(id+"F1.wireOp",EDGE,"E134.trimOffspring");var subQ59=sQuery(id+"F1.wireOp",EDGE,"E64.0");var subQ61=sQuery(id+"F1.wireOp",EDGE,"E137");var subQ62=sQuery(id+"F1.wireOp",EDGE,"E63.0");var subQ64=sQuery(id+"F1.wireOp",EDGE,"E135.trimOffspring");var subQ65=sQuery(id+"F1.wireOp",EDGE,"E62.0");var subQ71=sQuery(id+"F1.wireOp",EDGE,"E19.0");var subQ73=sQuery(id+"F1.wireOp",EDGE,"E58.0");var subQ75=sQuery(id+"F1.wireOp",EDGE,"E159");var subQ76=sQuery(id+"F1.wireOp",EDGE,"E9.0");var subQ78=sQuery(id+"F1.wireOp",EDGE,"E136.trimOffspring");var subQ79=sQuery(id+"F1.wireOp",EDGE,"E61.0");var subQ81=sQuery(id+"F1.wireOp",EDGE,"E162");var subQ82=sQuery(id+"F1.wireOp",EDGE,"E17.0");var subQ84=sQuery(id+"F1.wireOp",EDGE,"E56.0");var subQ86=sQuery(id+"F1.wireOp",EDGE,"E158.trimOffspring");var subQ87=sQuery(id+"F1.wireOp",EDGE,"E8.0");var subQ89=sQuery(id+"F1.wireOp",EDGE,"E133.trimOffspring");var subQ90=sQuery(id+"F1.wireOp",EDGE,"E60.0");var subQ92=sQuery(id+"F1.wireOp",EDGE,"E160");var subQ93=sQuery(id+"F1.wireOp",EDGE,"E15.0");var subQ95=sQuery(id+"F1.wireOp",EDGE,"E54.0");var subQ97=sQuery(id+"F1.wireOp",EDGE,"E125.trimOffspring");var subQ98=sQuery(id+"F1.wireOp",EDGE,"E7.0");var subQ100=sQuery(id+"F1.wireOp",EDGE,"E161");var subQ101=sQuery(id+"F1.wireOp",EDGE,"E59.0");var subQ103=sQuery(id+"F1.wireOp",EDGE,"E13.0");var subQ105=sQuery(id+"F1.wireOp",EDGE,"E52.0");var subQ107=sQuery(id+"F1.wireOp",EDGE,"E6.0");var subQ109=sQuery(id+"F1.wireOp",EDGE,"E129.trimOffspring");var subQ110=sQuery(id+"F1.wireOp",EDGE,"E156.trimOffspring");var subQ111=sQuery(id+"F1.wireOp",EDGE,"E11.0");var subQ113=sQuery(id+"F1.wireOp",EDGE,"E50.0");var subQ115=sQuery(id+"F1.wireOp",EDGE,"E5.0");var subQ116=sQuery(id+"F1.wireOp",EDGE,"E3");var subQ118=sQuery(id+"F1.wireOp",EDGE,"E132");var subQ119=sQuery(id+"F1.wireOp",EDGE,"E57.0");var subQ121=sQuery(id+"F1.wireOp",EDGE,"E48.0");var subQ123=sQuery(id+"F1.wireOp",EDGE,"E4");var subQ124=sQuery(id+"F1.wireOp",EDGE,"E130.trimOffspring");var subQ125=sQuery(id+"F1.wireOp",EDGE,"E46.0");var subQ127=sQuery(id+"F1.wireOp",EDGE,"E2");var subQ128=sQuery(id+"F1.wireOp",EDGE,"E128.trimOffspring");var subQ129=sQuery(id+"F1.wireOp",EDGE,"E55.0");var subQ131=sQuery(id+"F1.wireOp",EDGE,"E131");var subQ132=sQuery(id+"F1.wireOp",EDGE,"E157.trimOffspring");var subQ133=sQuery(id+"F1.wireOp",EDGE,"E51.0");var subQ135=sQuery(id+"F1.wireOp",EDGE,"E126.trimOffspring");var subQ136=sQuery(id+"F1.wireOp",EDGE,"E49.0");var subQ138=sQuery(id+"F1.wireOp",EDGE,"E24.0");var subQ140=sQuery(id+"F1.wireOp",EDGE,"E23.0");var subQ142=sQuery(id+"F1.wireOp",EDGE,"E22.0");var subQ144=sQuery(id+"F1.wireOp",EDGE,"E44.0");var subQ146=sQuery(id+"F1.wireOp",EDGE,"E20.0");var subQ148=sQuery(id+"F1.wireOp",EDGE,"E42.0");var subQ150=sQuery(id+"F1.wireOp",EDGE,"E40.0");var subQ152=sQuery(id+"F1.wireOp",EDGE,"E18.0");var subQ154=sQuery(id+"F1.wireOp",EDGE,"E38.0");var subQ156=sQuery(id+"F1.wireOp",EDGE,"E36.0");var subQ158=sQuery(id+"F1.wireOp",EDGE,"E16.0");var subQ160=sQuery(id+"F1.wireOp",EDGE,"E34.0");var subQ162=sQuery(id+"F1.wireOp",EDGE,"E14.0");var subQ164=sQuery(id+"F1.wireOp",EDGE,"E30.0");var subQ166=sQuery(id+"F1.wireOp",EDGE,"E127.trimOffspring");var subQ167=sQuery(id+"F1.wireOp",EDGE,"E28.0");var subQ169=sQuery(id+"F1.wireOp",EDGE,"E12.0");var subQ171=sQuery(id+"F1.wireOp",EDGE,"E26.0");var subQ173=sQuery(id+"F1.wireOp",EDGE,"E32.0");var subQ175=sQuery(id+"F1.wireOp",EDGE,"E53.0");var subQ177=sQuery(id+"F1.wireOp",EDGE,"E47.0");var subQ179=sQuery(id+"F1.wireOp",EDGE,"E10.0");var subQ181=sQuery(id+"F1.wireOp",EDGE,"E25.0");var subQ183=sQuery(id+"F1.wireOp",EDGE,"E27.0");var subQ185=sQuery(id+"F1.wireOp",EDGE,"E29.0");var subQ187=sQuery(id+"F1.wireOp",EDGE,"E31.0");var subQ189=sQuery(id+"F1.wireOp",EDGE,"E33.0");var subQ191=sQuery(id+"F1.wireOp",EDGE,"E35.0");var subQ193=sQuery(id+"F1.wireOp",EDGE,"E37.0");var subQ195=sQuery(id+"F1.wireOp",EDGE,"E39.0");var subQ197=sQuery(id+"F1.wireOp",EDGE,"E41.0");var subQ199=sQuery(id+"F1.wireOp",EDGE,"E43.0");var subQ201=sQuery(id+"F1.wireOp",EDGE,"E45.0");Q0=makeQuery(id+"F9.boolean.opBoolean","SPLIT",FACE,{"disambiguationData":[TD([makeQuery(id+"F2.opExtrude","SWEPT_FACE",FACE,{"disambiguationData":[OSD([subQ116])]})])],"derivedFrom":makeQuery(id+"F2.opExtrude","CAP_FACE",FACE,{"disambiguationData":[OSD([sQuery(id+"F1.wireOp",EDGE,"E1"),subQ127,subQ116,subQ123,subQ115,subQ107,subQ98,subQ87,subQ76,subQ179,subQ111,subQ169,subQ103,subQ162,subQ93,subQ158,subQ82,subQ152,subQ71,subQ146,subQ142,subQ140,subQ138,subQ181,subQ171,subQ183,subQ167,subQ185,subQ164,subQ187,subQ173,subQ189,subQ160,subQ191,subQ156,subQ193,subQ154,subQ195,subQ150,subQ197,subQ148,subQ199,subQ144,subQ201,subQ125,subQ177,subQ121,subQ136,subQ113,subQ133,subQ105,subQ175,subQ95,subQ129,subQ84,subQ119,subQ73,subQ101,subQ90,subQ79,subQ65,subQ62,subQ59,subQ56,subQ53,subQ50,subQ47,subQ44,subQ41,subQ38,subQ35,subQ32,subQ29,subQ26,subQ23,subQ20,subQ17,subQ14,subQ11,subQ8,subQ5,subQ1,sQuery(id+"F1.wireOp",EDGE,"E84"),subQ2,sQuery(id+"F1.wireOp",EDGE,"E86.trimOffspring"),sQuery(id+"F1.wireOp",EDGE,"E87.trimOffspring"),sQuery(id+"F1.wireOp",EDGE,"E88.trimOffspring"),sQuery(id+"F1.wireOp",EDGE,"E89.trimOffspring"),sQuery(id+"F1.wireOp",EDGE,"E90.trimOffspring"),sQuery(id+"F1.wireOp",EDGE,"E91.trimOffspring"),sQuery(id+"F1.wireOp",EDGE,"E92.trimOffspring"),sQuery(id+"F1.wireOp",EDGE,"E93.trimOffspring"),sQuery(id+"F1.wireOp",EDGE,"E94.trimOffspring"),sQuery(id+"F1.wireOp",EDGE,"E95.trimOffspring"),sQuery(id+"F1.wireOp",EDGE,"E96.trimOffspring"),sQuery(id+"F1.wireOp",EDGE,"E97.trimOffspring"),sQuery(id+"F1.wireOp",EDGE,"E98.trimOffspring"),sQuery(id+"F1.wireOp",EDGE,"E99.trimOffspring"),sQuery(id+"F1.wireOp",EDGE,"E100.trimOffspring"),sQuery(id+"F1.wireOp",EDGE,"E101.trimOffspring"),sQuery(id+"F1.wireOp",EDGE,"E102.trimOffspring"),sQuery(id+"F1.wireOp",EDGE,"E103.trimOffspring"),sQuery(id+"F1.wireOp",EDGE,"E104.trimOffspring"),sQuery(id+"F1.wireOp",EDGE,"E105.trimOffspring"),sQuery(id+"F1.wireOp",EDGE,"E106.trimOffspring"),sQuery(id+"F1.wireOp",EDGE,"E107.trimOffspring"),sQuery(id+"F1.wireOp",EDGE,"E108.trimOffspring"),sQuery(id+"F1.wireOp",EDGE,"E109.trimOffspring"),sQuery(id+"F1.wireOp",EDGE,"E110.trimOffspring"),sQuery(id+"F1.wireOp",EDGE,"E111.trimOffspring"),sQuery(id+"F1.wireOp",EDGE,"E112.trimOffspring"),sQuery(id+"F1.wireOp",EDGE,"E113.trimOffspring"),sQuery(id+"F1.wireOp",EDGE,"E114.trimOffspring"),sQuery(id+"F1.wireOp",EDGE,"E115.trimOffspring"),sQuery(id+"F1.wireOp",EDGE,"E116.trimOffspring"),sQuery(id+"F1.wireOp",EDGE,"E117.trimOffspring"),sQuery(id+"F1.wireOp",EDGE,"E118.trimOffspring"),sQuery(id+"F1.wireOp",EDGE,"E119.trimOffspring"),sQuery(id+"F1.wireOp",EDGE,"E120.trimOffspring"),sQuery(id+"F1.wireOp",EDGE,"E121.trimOffspring"),sQuery(id+"F1.wireOp",EDGE,"E122.trimOffspring"),sQuery(id+"F1.wireOp",EDGE,"E123.trimOffspring"),sQuery(id+"F1.wireOp",EDGE,"E124.trimOffspring"),subQ97,subQ135,subQ166,subQ128,subQ109,subQ124,subQ131,subQ118,subQ89,subQ58,subQ64,subQ78,subQ61,subQ52,subQ46,subQ49,subQ55,subQ43,subQ40,subQ34,subQ28,subQ31,subQ25,subQ22,subQ19,subQ10,subQ0,subQ16,subQ13,subQ4,subQ7,subQ110,subQ132,subQ86,subQ75,subQ92,subQ100,subQ81,subQ37])],"isStart":false})});}
            var sketch = newSketch(context, id + "F13", { "sketchPlane" : qUnion([Q0])});
            skLineSegment(sketch, "E212", {"start": v(-20201.46, 3851) * mm, "end": v(-16976.46, 3851) * mm});
            skLineSegment(sketch, "E213", {"start": v(-8476.46, 3851) * mm, "end": v(-8476.46, 4201) * mm});
            skLineSegment(sketch, "E214", {"start": v(-8476.46, 4201) * mm, "end": v(-15926.46, 4201) * mm});
            skLineSegment(sketch, "E215", {"start": v(-20201.46, 4201) * mm, "end": v(-20201.46, 3851) * mm});
            skLineSegment(sketch, "E216", {"start": v(-16976.46, 3851) * mm, "end": v(-16976.46, 3651) * mm});
            skLineSegment(sketch, "E217", {"start": v(-15926.46, 3851) * mm, "end": v(-15926.46, 3651) * mm});
            skLineSegment(sketch, "E218.trimOffspring", {"start": v(-15926.46, 3851) * mm, "end": v(-8476.46, 3851) * mm});
            skArc(sketch, "E219", {"start": v(-15926.46, 4201) * mm, "mid": v(-16252.3, 4094.1) * mm, "end": v(-16451.46, 3814.94) * mm});
            skArc(sketch, "E220", {"start": v(-16451.46, 3814.94) * mm, "mid": v(-16650.63, 4094.1) * mm, "end": v(-16976.46, 4201) * mm});
            skLineSegment(sketch, "E221.trimOffspring", {"start": v(-16976.46, 4201) * mm, "end": v(-20201.46, 4201) * mm});
            skPoint(sketch, "E222.end.orphan", {"position": v(-16451.46, 3651) * mm});
            skLineSegment(sketch, "E223", {"start": v(-16976.46, 3651) * mm, "end": v(-15926.46, 3651) * mm});
            skSolve(sketch);
        }
        {
            var Q0;
            Q0=makeQuery(id+"F13.imprint","IMPRINT",FACE,{"disambiguationData":[TD([[makeQuery(id+"F13.imprint","IMPRINT",EDGE,{"derivedFrom":sQuery(id+"F13.wireOp",EDGE,"E212")}),1.0]])]});
            extrude(context, id + "F14", {"entities" : qUnion([Q0]), "operationType" : NewBodyOperationType.ADD, "depth" : 500 * mm, "offsetDistance" : 25 * mm});
        }
        {
            var Q0;
            Q0=qSketchRegion(id+"F12",true);
            extrude(context, id + "F15", {"entities" : qUnion([Q0]), "oppositeDirection" : true, "depth" : 500 * mm, "offsetDistance" : 25 * mm});
        }
        {
            var Q0;
            Q0=makeQuery(id+"F15.opExtrude","CAP_FACE",FACE,{"disambiguationData":[OSD([sQuery(id+"F12.wireOp",EDGE,"E190"),sQuery(id+"F12.wireOp",EDGE,"E191"),sQuery(id+"F12.wireOp",EDGE,"E192"),sQuery(id+"F12.wireOp",EDGE,"E193"),sQuery(id+"F12.wireOp",EDGE,"E194.filletArc"),sQuery(id+"F12.wireOp",EDGE,"E195.filletArc"),sQuery(id+"F12.wireOp",EDGE,"E196"),sQuery(id+"F12.wireOp",EDGE,"E197"),sQuery(id+"F12.wireOp",EDGE,"E198"),sQuery(id+"F12.wireOp",EDGE,"E199")])],"isStart":true});
            var sketch = newSketch(context, id + "F16", { "sketchPlane" : qUnion([Q0])});
            skLineSegment(sketch, "E224", {"start": v(-14051.46, 4551) * mm, "end": v(-14051.46, 4901) * mm});
            skLineSegment(sketch, "E225", {"start": v(-14051.46, 4901) * mm, "end": v(-13551.46, 4901) * mm});
            skLineSegment(sketch, "E226", {"start": v(-13551.46, 4901) * mm, "end": v(-13551.46, 4551) * mm});
            skLineSegment(sketch, "E227", {"start": v(-13551.46, 4551) * mm, "end": v(-14051.46, 4551) * mm});
            skLineSegment(sketch, "E228", {"start": v(-14051.46, 4551) * mm, "end": v(-16201.46, 4551) * mm});
            skLineSegment(sketch, "E229", {"start": v(-16201.46, 4551) * mm, "end": v(-16201.46, 2846.64) * mm});
            skLineSegment(sketch, "E230.MirrorCS", {"start": v(-18851.46, 4551) * mm, "end": v(-18351.46, 4551) * mm});
            skLineSegment(sketch, "E231.MirrorCS", {"start": v(-18351.46, 4551) * mm, "end": v(-18351.46, 4901) * mm});
            skLineSegment(sketch, "E232.MirrorCS", {"start": v(-18351.46, 4901) * mm, "end": v(-18851.46, 4901) * mm});
            skLineSegment(sketch, "E233.MirrorCS", {"start": v(-18851.46, 4901) * mm, "end": v(-18851.46, 4551) * mm});
            skSolve(sketch);
        }
        {
            var Q0;
            Q0=makeQuery(id+"F16.imprint","IMPRINT",FACE,{"disambiguationData":[TD([[makeQuery(id+"F16.imprint","IMPRINT",EDGE,{"derivedFrom":sQuery(id+"F16.wireOp",EDGE,"E230.MirrorCS")}),1.0]])]});
            var Q1;
            Q1=makeQuery(id+"F16.imprint","IMPRINT",FACE,{"disambiguationData":[TD([[makeQuery(id+"F16.imprint","IMPRINT",EDGE,{"derivedFrom":sQuery(id+"F16.wireOp",EDGE,"E224")}),-1.0]])]});
            extrude(context, id + "F17", {"entities" : qUnion([Q0, Q1]), "oppositeDirection" : true, "depth" : 544 * mm, "offsetDistance" : 25 * mm});
        }
    });
